FCSTD DOCUMENT  (FreeCAD 1.2R20260204 (Git shallow))
Label: RC-Robot-structure-asm
License: All rights reserved
LicenseURL: https://en.wikipedia.org/wiki/All_rights_reserved
objects: App::FeaturePython×108, App::Link×35, App::Point×1, Assembly::JointGroup×1, Assembly::AssemblyObject×1
EXTERNAL_REF file=RC-Robot-parts-export.FCStd obj=Part__Feature010
EXTERNAL_REF file=RC-Robot-parts-export.FCStd obj=Part__Feature011
EXTERNAL_REF file=RC-Robot-parts-export.FCStd obj=Part__Feature012
EXTERNAL_REF file=RC-Robot-parts-export.FCStd obj=Part__Mirroring006
EXTERNAL_REF file=RC-Robot-parts-export.FCStd obj=Part__Feature013
EXTERNAL_REF file=RC-Robot-parts-export.FCStd obj=Part__Feature015
EXTERNAL_REF file=RC-Robot-parts-export.FCStd obj=Part__Mirroring
EXTERNAL_REF file=RC-Robot-parts-export.FCStd obj=Part__Mirroring004
EXTERNAL_REF file=RC-Robot-parts-export.FCStd obj=Part__Mirroring005
EXTERNAL_REF file=RC-Robot-parts-export.FCStd obj=Part__Feature016
EXTERNAL_REF file=RC-Robot-parts-export.FCStd obj=Part__Mirroring002
EXTERNAL_REF file=RC-Robot-parts-export.FCStd obj=Part__Feature017
EXTERNAL_REF file=RC-Robot-parts-export.FCStd obj=Part__Mirroring001
EXTERNAL_REF file=RC-Robot-parts-export.FCStd obj=Part__Feature009
EXTERNAL_REF file=RC-Robot-parts-export.FCStd obj=Part
EXTERNAL_REF file=actuators-parts/wheel.FCStd obj=Part001
EXTERNAL_REF file=RC-Robot-parts-export.FCStd obj=Part__Feature004
EXTERNAL_REF file=mecanical-parts/free-wheel-support.FCStd obj=Body

FEATURE [App::Point] Origin001  label="Origine"
  Role = Origin
FEATURE [App::Link] _2020_50mm  label="2020-50mm"
  LinkPlacement = pos=(-141,2.85605,40.8027) rot=(-1,0,0;0.09388rad)
  LinkedObject = -> <external RC-Robot-parts-export.FCStd>#Part__Feature010
  Placement = pos=(-141,2.85605,40.8027) rot=(-1,0,0;0.09388rad)
FEATURE [App::Link] _2020_50mm001  label="2020-50mm001"
  LinkPlacement = pos=(-190,332.398,9.77417) rot=(0.046871,0.046871,0.997801;4.71019rad)
  LinkedObject = -> <external RC-Robot-parts-export.FCStd>#Part__Feature010
  Placement = pos=(-190,332.398,9.77417) rot=(0.046871,0.046871,0.997801;4.71019rad)
FEATURE [App::Link] _2020_300mm  label="2020-300mm"
  LinkPlacement = pos=(-176,170,-7.361e-13) rot=(1,0,0;4.71239rad)
  LinkedObject = -> <external RC-Robot-parts-export.FCStd>#Part__Feature011
  Placement = pos=(-176,170,-7.361e-13) rot=(1,0,0;4.71239rad)
FEATURE [App::Link] _2020_300mm001  label="2020-300mm001"
  LinkPlacement = pos=(-176,174.679,49.6896) rot=(1,0,0;1.38304rad)
  LinkedObject = -> <external RC-Robot-parts-export.FCStd>#Part__Feature011
  Placement = pos=(-176,174.679,49.6896) rot=(1,0,0;1.38304rad)
FEATURE [App::Link] _2020_300mm002  label="2020-300mm002"
  LinkPlacement = pos=(-556,170,-4.884e-13) rot=(-1,0,0;1.5708rad)
  LinkedObject = -> <external RC-Robot-parts-export.FCStd>#Part__Feature011
  Placement = pos=(-556,170,-4.884e-13) rot=(-1,0,0;1.5708rad)
FEATURE [App::Link] _2020_300mm003  label="2020-300mm003"
  LinkPlacement = pos=(-556,174.679,49.6896) rot=(1,0,0;4.52463rad)
  LinkedObject = -> <external RC-Robot-parts-export.FCStd>#Part__Feature011
  Placement = pos=(-556,174.679,49.6896) rot=(1,0,0;4.52463rad)
FEATURE [App::Link] _2020_300mm004  label="2020-300mm004"
  LinkPlacement = pos=(-286,170,2.72e-14) rot=(-1,0,0;1.5708rad)
  LinkedObject = -> <external RC-Robot-parts-export.FCStd>#Part__Feature011
  Placement = pos=(-286,170,2.72e-14) rot=(-1,0,0;1.5708rad)
FEATURE [App::Link] _2020_300mm005  label="2020-300mm005"
  LinkPlacement = pos=(-446,170,-2.7e-15) rot=(1,0,0;4.71239rad)
  LinkedObject = -> <external RC-Robot-parts-export.FCStd>#Part__Feature011
  Placement = pos=(-446,170,-2.7e-15) rot=(1,0,0;4.71239rad)
FEATURE [App::Link] _2020_300mm006  label="2020-300mm006"
  LinkPlacement = pos=(-286,174.679,49.6896) rot=(1,0,0;4.52463rad)
  LinkedObject = -> <external RC-Robot-parts-export.FCStd>#Part__Feature011
  Placement = pos=(-286,174.679,49.6896) rot=(1,0,0;4.52463rad)
FEATURE [App::Link] _2020_300mm007  label="2020-300mm007"
  LinkPlacement = pos=(-446,174.679,49.6896) rot=(1,0,0;4.52463rad)
  LinkedObject = -> <external RC-Robot-parts-export.FCStd>#Part__Feature011
  Placement = pos=(-446,174.679,49.6896) rot=(1,0,0;4.52463rad)
FEATURE [App::Link] _2020_340mm  label="2020-340mm"
  LinkPlacement = pos=(6.41e-14,-403,-5.59e-14) rot=(0.57735,0.57735,0.57735;2.0944rad)
  LinkedObject = -> <external RC-Robot-parts-export.FCStd>#Part__Feature012
  Placement = pos=(6.41e-14,-403,-5.59e-14) rot=(0.57735,0.57735,0.57735;2.0944rad)
FEATURE [App::Link] _2020_340mm001  label="2020-340mm001"
  LinkPlacement = pos=(1.53e-14,-67.5569,-314.496) rot=(0.093333,0.991251,-0.093333;4.7036rad)
  LinkedObject = -> <external RC-Robot-parts-export.FCStd>#Part__Feature012
  Placement = pos=(1.53e-14,-67.5569,-314.496) rot=(0.093333,0.991251,-0.093333;4.7036rad)
FEATURE [App::Link] _2020_340mm002  label="2020-340mm002"
  LinkPlacement = pos=(1.04e-14,312.134,-393.1) rot=(0.046871,0.997801,-0.046871;4.71019rad)
  LinkedObject = -> <external RC-Robot-parts-export.FCStd>#Part__Feature012
  Placement = pos=(1.04e-14,312.134,-393.1) rot=(0.046871,0.997801,-0.046871;4.71019rad)
FEATURE [App::FeaturePython] Joint  label="Fixed"  # Assembly joint (typed FeaturePython)
  Angle = 0
  AngleMax = 0
  AngleMin = 0
  Detach1 = false
  Detach2 = false
  Distance = 0
  Distance2 = 0
  EnableAngleMax = false
  EnableAngleMin = false
  EnableLengthMax = false
  EnableLengthMin = false
  JointType = 0 (Fixed)
  LengthMax = 0
  LengthMin = 0
  Offset2 = pos=(0,0,170) rot=(0,0,1;0rad)
  Placement1 = pos=(403,1.007e-13,170) rot=(0,0,1;0rad)
  Placement2 = pos=(0,0,170) rot=(0,0,1;0rad)
  Reference1 = -> _2020_340mm [Face50,Edge6]
  Reference2 = -> Origin [YZ_Plane.,YZ_Plane.]
  Suppressed = false
FEATURE [App::FeaturePython] GroundedJoint  # Assembly grounded joint (typed FeaturePython)
  ObjectToGround = -> _2020_340mm
FEATURE [App::Link] CoinLateralBD
  LinkPlacement = pos=(180,64.583,-54.9907) rot=(0.046871,-0.046871,0.997801;1.573rad)
  LinkedObject = -> <external RC-Robot-parts-export.FCStd>#Part__Mirroring006
  Placement = pos=(180,64.583,-54.9907) rot=(0.046871,-0.046871,0.997801;1.573rad)
FEATURE [App::FeaturePython] Joint001  label="Revolute002"  # Assembly joint (typed FeaturePython)
  Angle = 0
  AngleMax = 0
  AngleMin = 0
  Detach1 = false
  Detach2 = false
  Distance = 0
  Distance2 = 0
  EnableAngleMax = false
  EnableAngleMin = false
  EnableLengthMax = false
  EnableLengthMin = false
  JointType = 1 (Revolute)
  LengthMax = 0
  LengthMin = 0
  Placement1 = pos=(-59.1437,10,60.8027) rot=(0.066432,-0.705545,0.705545;3.00892rad)
  Placement2 = pos=(403,1.007e-13,170) rot=(0,0,1;0rad)
  Reference1 = -> CoinLateralBD [Edge7,Edge7]
  Reference2 = -> _2020_340mm [Edge52,Edge52]
  Suppressed = false
FEATURE [App::FeaturePython] Joint002  label="Parallel002"  # Assembly joint (typed FeaturePython)
  Angle = 0
  AngleMax = 0
  AngleMin = 0
  Detach1 = false
  Detach2 = false
  Distance = 0
  Distance2 = 0
  EnableAngleMax = false
  EnableAngleMin = false
  EnableLengthMax = false
  EnableLengthMin = false
  JointType = 6 (Parallel)
  LengthMax = 0
  LengthMin = 0
  Placement1 = pos=(-68.1623,30,71.6961) rot=(-0.046923,0,-0.998899;3.14159rad)
  Placement2 = pos=(398.1,10,170) rot=(-0.57735,-0.57735,-0.57735;2.0944rad)
  Reference1 = -> CoinLateralBD [Face8,Vertex15]
  Reference2 = -> _2020_340mm [Face22,Vertex40]
  Suppressed = false
FEATURE [App::FeaturePython] Joint004  label="Distance002"  # Assembly joint (typed FeaturePython)
  Angle = 0
  AngleMax = 0
  AngleMin = 0
  Detach1 = false
  Detach2 = false
  Distance = 0
  Distance2 = 0
  EnableAngleMax = false
  EnableAngleMin = false
  EnableLengthMax = false
  EnableLengthMin = false
  JointType = 5 (Distance)
  LengthMax = 0
  LengthMin = 0
  Placement1 = pos=(321,6.7,7.1e-15) rot=(0,1,0;1.5708rad)
  Placement2 = pos=(-58.1674,3.411e-13,86.3477) rot=(0.505206,0.610232,-0.610232;2.20599rad)
  Reference1 = -> _2020_50mm [Face26,Vertex37]
  Reference2 = -> CoinLateralBD [Face28,Face28]
  Suppressed = false
FEATURE [App::FeaturePython] Joint005  label="Distance003"  # Assembly joint (typed FeaturePython)
  Angle = 0
  AngleMax = 0
  AngleMin = 0
  Detach1 = false
  Detach2 = false
  Distance = 0
  Distance2 = 0
  EnableAngleMax = false
  EnableAngleMin = false
  EnableLengthMax = false
  EnableLengthMin = false
  JointType = 5 (Distance)
  LengthMax = 0
  LengthMin = 0
  Placement1 = pos=(331,1.13e-14,-25) rot=(0,0,1;0rad)
  Placement2 = pos=(-57.1418,-10,76.5974) rot=(0,-1,0;2.95383rad)
  Reference1 = -> _2020_50mm [Face51,Vertex66]
  Reference2 = -> CoinLateralBD [Face19,Face19]
  Suppressed = false
FEATURE [App::FeaturePython] Joint006  label="Distance004"  # Assembly joint (typed FeaturePython)
  Angle = 0
  AngleMax = 0
  AngleMin = 0
  Detach1 = false
  Detach2 = false
  Distance = 0
  Distance2 = 0
  EnableAngleMax = false
  EnableAngleMin = false
  EnableLengthMax = false
  EnableLengthMin = false
  JointType = 5 (Distance)
  LengthMax = 0
  LengthMin = 0
  Placement1 = pos=(-45.4509,-10,84.5551) rot=(0,1,0;1.75856rad)
  Placement2 = pos=(337.7,10,-7.1e-15) rot=(0.57735,0.57735,0.57735;4.18879rad)
  Reference1 = -> CoinLateralBD [Face20,Edge1]
  Reference2 = -> _2020_50mm [Face2,Vertex54]
  Suppressed = false
FEATURE [App::FeaturePython] Joint007  label="Distance006"  # Assembly joint (typed FeaturePython)
  Angle = 0
  AngleMax = 0
  AngleMin = 0
  Detach1 = false
  Detach2 = false
  Distance = 0
  Distance2 = 0
  EnableAngleMax = false
  EnableAngleMin = false
  EnableLengthMax = false
  EnableLengthMin = false
  JointType = 5 (Distance)
  LengthMax = 0
  LengthMin = 0
  Placement1 = pos=(366,4.6e-15,-150) rot=(0,0,1;0rad)
  Placement2 = pos=(-39.2318,-10,58.9279) rot=(0,-1,0;1.47692rad)
  Reference1 = -> _2020_300mm [Face51,Vertex62]
  Reference2 = -> CoinLateralBD [Face18,Face18]
  Suppressed = false
FEATURE [App::FeaturePython] Joint008  label="Distance007"  # Assembly joint (typed FeaturePython)
  Angle = 0
  AngleMax = 0
  AngleMin = 0
  Detach1 = false
  Detach2 = false
  Distance = 0
  Distance2 = 0
  EnableAngleMax = false
  EnableAngleMin = false
  EnableLengthMax = false
  EnableLengthMin = false
  JointType = 5 (Distance)
  LengthMax = 0
  LengthMin = 0
  Placement1 = pos=(359.3,-10,4.547e-13) rot=(0.57735,0.57735,0.57735;4.18879rad)
  Placement2 = pos=(-28.3384,-10,67.9464) rot=(0,1,0;0.09388rad)
  Reference1 = -> _2020_300mm [Face49,Vertex100]
  Reference2 = -> CoinLateralBD [Face21,Vertex44]
  Suppressed = false
FEATURE [App::FeaturePython] Joint009  label="Distance008"  # Assembly joint (typed FeaturePython)
  Angle = 0
  AngleMax = 0
  AngleMin = 0
  Detach1 = false
  Detach2 = false
  Distance = 0
  Distance2 = 0
  EnableAngleMax = false
  EnableAngleMin = false
  EnableLengthMax = false
  EnableLengthMin = false
  JointType = 5 (Distance)
  LengthMax = 0
  LengthMin = 0
  Placement1 = pos=(376,-6.7,4.832e-13) rot=(0,-1,0;1.5708rad)
  Placement2 = pos=(-45.367,-20,69.775) rot=(0.505206,0.610232,-0.610232;2.20599rad)
  Reference1 = -> _2020_300mm [Face25,Vertex77]
  Reference2 = -> CoinLateralBD [Face11,Face11]
  Suppressed = false
FEATURE [App::Link] CoinLateralHD
  LinkPlacement = pos=(180,64.583,34.9907) rot=(-0.046871,0.046871,0.997801;1.573rad)
  LinkedObject = -> <external RC-Robot-parts-export.FCStd>#Part__Feature013
  Placement = pos=(180,64.583,34.9907) rot=(-0.046871,0.046871,0.997801;1.573rad)
FEATURE [App::FeaturePython] Joint010  label="Distance009"  # Assembly joint (typed FeaturePython)
  Angle = 0
  AngleMax = 0
  AngleMin = 0
  Detach1 = false
  Detach2 = false
  Distance = 0
  Distance2 = 0
  EnableAngleMax = false
  EnableAngleMin = false
  EnableLengthMax = false
  EnableLengthMin = false
  JointType = 5 (Distance)
  LengthMax = 0
  LengthMin = 0
  Placement1 = pos=(-62,-10,25) rot=(0,-1,0;3.14159rad)
  Placement2 = pos=(331,-4.9e-15,25) rot=(0,1,0;3.14159rad)
  Reference1 = -> CoinLateralHD [Face19,Face19]
  Reference2 = -> _2020_50mm [Face1,Vertex8]
  Suppressed = false
FEATURE [App::FeaturePython] Joint011  label="Distance010"  # Assembly joint (typed FeaturePython)
  Angle = 0
  AngleMax = 0
  AngleMin = 0
  Detach1 = false
  Detach2 = false
  Distance = 0
  Distance2 = 0
  EnableAngleMax = false
  EnableAngleMin = false
  EnableLengthMax = false
  EnableLengthMin = false
  JointType = 5 (Distance)
  LengthMax = 0
  LengthMin = 0
  Placement1 = pos=(-49.1588,-20,29.5047) rot=(-0.57735,-0.57735,-0.57735;2.0944rad)
  Placement2 = pos=(341,6.7,-2.13e-14) rot=(0,-1,0;1.5708rad)
  Reference1 = -> CoinLateralHD [Face11,Vertex24]
  Reference2 = -> _2020_50mm [Face5,Vertex3]
  Suppressed = false
FEATURE [App::FeaturePython] Joint012  label="Distance011"  # Assembly joint (typed FeaturePython)
  Angle = 0
  AngleMax = 0
  AngleMin = 0
  Detach1 = false
  Detach2 = false
  Distance = 0
  Distance2 = 0
  EnableAngleMax = false
  EnableAngleMin = false
  EnableLengthMax = false
  EnableLengthMin = false
  JointType = 5 (Distance)
  LengthMax = 0
  LengthMin = 0
  Placement1 = pos=(-72,10.4414,17.0721) rot=(-0.57735,-0.57735,0.57735;2.0944rad)
  Placement2 = pos=(324.3,-10,-1.42e-14) rot=(0.57735,0.57735,0.57735;4.18879rad)
  Reference1 = -> CoinLateralHD [Face25,Face25]
  Reference2 = -> _2020_50mm [Face49,Vertex26]
  Suppressed = false
FEATURE [App::FeaturePython] Joint013  label="Parallel004"  # Assembly joint (typed FeaturePython)
  Angle = 0
  AngleMax = 0
  AngleMin = 0
  Detach1 = false
  Detach2 = false
  Distance = 0
  Distance2 = 0
  EnableAngleMax = false
  EnableAngleMin = false
  EnableLengthMax = false
  EnableLengthMin = false
  JointType = 6 (Parallel)
  LengthMax = 0
  LengthMin = 0
  Placement1 = pos=(368.84,-3.9,150) rot=(0,1,0;3.14159rad)
  Placement2 = pos=(-41.1066,-10,39.0159) rot=(0,-1,0;4.61851rad)
  Reference1 = -> _2020_300mm001 [Face1,Vertex20]
  Reference2 = -> CoinLateralHD [Face18,Face18]
  Suppressed = false
FEATURE [App::FeaturePython] Joint014  label="Distance014"  # Assembly joint (typed FeaturePython)
  Angle = 0
  AngleMax = 0
  AngleMin = 0
  Detach1 = false
  Detach2 = false
  Distance = 0
  Distance2 = 0
  EnableAngleMax = false
  EnableAngleMin = false
  EnableLengthMax = false
  EnableLengthMin = false
  JointType = 5 (Distance)
  LengthMax = 0
  LengthMin = 0
  Placement1 = pos=(376,-6.7,4.547e-13) rot=(0,-1,0;1.5708rad)
  Placement2 = pos=(-49.1588,-20,29.5047) rot=(-0.57735,-0.57735,-0.57735;2.0944rad)
  Reference1 = -> _2020_300mm001 [Face25,Vertex14]
  Reference2 = -> CoinLateralHD [Face11,Vertex21]
  Suppressed = false
FEATURE [App::FeaturePython] Joint015  label="Distance015"  # Assembly joint (typed FeaturePython)
  Angle = 0
  AngleMax = 0
  AngleMin = 0
  Detach1 = false
  Detach2 = false
  Distance = 0
  Distance2 = 0
  EnableAngleMax = false
  EnableAngleMin = false
  EnableLengthMax = false
  EnableLengthMin = false
  JointType = 5 (Distance)
  LengthMax = 0
  LengthMin = 0
  Placement1 = pos=(-32.0881,-10,28.1226) rot=(0,1,0;0.09388rad)
  Placement2 = pos=(372.7,-10,-4.832e-13) rot=(-0.57735,-0.57735,-0.57735;2.0944rad)
  Reference1 = -> CoinLateralHD [Face21,Vertex44]
  Reference2 = -> _2020_300mm001 [Face29,Vertex15]
  Suppressed = false
FEATURE [App::FeaturePython] Joint016  label="Distance016"  # Assembly joint (typed FeaturePython)
  Angle = 0
  AngleMax = 0
  AngleMin = 0
  Detach1 = false
  Detach2 = false
  Distance = 0
  Distance2 = 0
  EnableAngleMax = false
  EnableAngleMin = false
  EnableLengthMax = false
  EnableLengthMin = false
  JointType = 5 (Distance)
  LengthMax = 0
  LengthMin = 0
  Placement1 = pos=(366,-1.42e-14,150) rot=(0,1,0;3.14159rad)
  Placement2 = pos=(-41.1066,-10,39.0159) rot=(0,-1,0;4.61851rad)
  Reference1 = -> _2020_300mm001 [Face1,Edge2]
  Reference2 = -> CoinLateralHD [Face18,Face18]
  Suppressed = false
FEATURE [App::FeaturePython] Joint017  label="Parallel005"  # Assembly joint (typed FeaturePython)
  Angle = 0
  AngleMax = 0
  AngleMin = 0
  Detach1 = false
  Detach2 = false
  Distance = 0
  Distance2 = 0
  EnableAngleMax = false
  EnableAngleMin = false
  EnableLengthMax = false
  EnableLengthMin = false
  JointType = 6 (Parallel)
  LengthMax = 0
  LengthMin = 0
  Placement1 = pos=(407.9,-10,-170) rot=(0.57735,0.57735,0.57735;4.18879rad)
  Placement2 = pos=(-70.9745,-5,41.8282) rot=(0.673149,0,-0.739507;3.14159rad)
  Reference1 = -> _2020_340mm001 [Face29,Vertex81]
  Reference2 = -> CoinLateralHD [Face7,Face7]
  Suppressed = false
FEATURE [App::FeaturePython] Joint018  label="Distance017"  # Assembly joint (typed FeaturePython)
  Angle = 0
  AngleMax = 0
  AngleMin = 0
  Detach1 = false
  Detach2 = false
  Distance = 0
  Distance2 = 0
  EnableAngleMax = false
  EnableAngleMin = false
  EnableLengthMax = false
  EnableLengthMin = false
  JointType = 5 (Distance)
  LengthMax = 0
  LengthMin = 0
  Placement1 = pos=(409.7,-10,-5.945e-13) rot=(0.57735,0.57735,0.57735;4.18879rad)
  Placement2 = pos=(-70.9745,-5,41.8282) rot=(0.673149,0,-0.739507;3.14159rad)
  Reference1 = -> _2020_340mm001 [Face29,Vertex79]
  Reference2 = -> CoinLateralHD [Face7,Face7]
  Suppressed = false
FEATURE [App::FeaturePython] Joint019  label="Distance018"  # Assembly joint (typed FeaturePython)
  Angle = 0
  AngleMax = 0
  AngleMin = 0
  Detach1 = false
  Detach2 = false
  Distance = 0
  Distance2 = 0
  EnableAngleMax = false
  EnableAngleMin = false
  EnableLengthMax = false
  EnableLengthMin = false
  JointType = 5 (Distance)
  LengthMax = 0
  LengthMin = 0
  Placement1 = pos=(393,-6.7,-1.13e-14) rot=(0,1,0;1.5708rad)
  Placement2 = pos=(-61.956,20,30.9348) rot=(-0.046923,0,-0.998899;3.14159rad)
  Reference1 = -> _2020_340mm001 [Face46,Vertex96]
  Reference2 = -> CoinLateralHD [Face8,Face8]
  Suppressed = false
FEATURE [App::FeaturePython] Joint020  label="Distance019"  # Assembly joint (typed FeaturePython)
  Angle = 0
  AngleMax = 0
  AngleMin = 0
  Detach1 = false
  Detach2 = false
  Distance = 0
  Distance2 = 0
  EnableAngleMax = false
  EnableAngleMin = false
  EnableLengthMax = false
  EnableLengthMin = false
  JointType = 5 (Distance)
  LengthMax = 0
  LengthMin = 0
  Placement1 = pos=(403,-1.87e-14,-170) rot=(0,0,1;0rad)
  Placement2 = pos=(-61.0185,10,40.8908) rot=(-0.57735,-0.57735,-0.57735;2.0944rad)
  Reference1 = -> _2020_340mm001 [Face51,Edge2]
  Reference2 = -> CoinLateralHD [Face5,Vertex7]
  Suppressed = false
FEATURE [App::Link] CoinAvant001
  LinkPlacement = pos=(180,64.583,34.9907) rot=(-0.046871,0.046871,0.997801;1.573rad)
  LinkedObject = -> <external RC-Robot-parts-export.FCStd>#Part__Feature015
  Placement = pos=(180,64.583,34.9907) rot=(-0.046871,0.046871,0.997801;1.573rad)
FEATURE [App::FeaturePython] Joint040  label="Distance040"  # Assembly joint (typed FeaturePython)
  Angle = 0
  AngleMax = 0
  AngleMin = 0
  Detach1 = false
  Detach2 = false
  Distance = 0
  Distance2 = 0
  EnableAngleMax = false
  EnableAngleMin = false
  EnableLengthMax = false
  EnableLengthMin = false
  JointType = 5 (Distance)
  LengthMax = 0
  LengthMin = 0
  Placement1 = pos=(257.479,-10,-9.89779) rot=(0,1,0;1.47692rad)
  Placement2 = pos=(366,-8.5e-15,150) rot=(0,1,0;3.14159rad)
  Reference1 = -> CoinAvant001 [Face32,Vertex62]
  Reference2 = -> _2020_300mm [Face1,Edge26]
  Suppressed = false
FEATURE [App::FeaturePython] Joint041  label="Distance041"  # Assembly joint (typed FeaturePython)
  Angle = 0
  AngleMax = 0
  AngleMin = 0
  Detach1 = false
  Detach2 = false
  Distance = 0
  Distance2 = 0
  EnableAngleMax = false
  EnableAngleMin = false
  EnableLengthMax = false
  EnableLengthMin = false
  JointType = 5 (Distance)
  LengthMax = 0
  LengthMin = 0
  Placement1 = pos=(247.472,5.68e-14,1.91918e-11) rot=(-0.57735,-0.57735,-0.57735;2.0944rad)
  Placement2 = pos=(356,6.7,-2.84e-14) rot=(0,1,0;1.5708rad)
  Reference1 = -> CoinAvant001 [Face25,Face25]
  Reference2 = -> _2020_300mm [Face26,Vertex38]
  Suppressed = false
FEATURE [App::FeaturePython] Joint042  label="Distance042"  # Assembly joint (typed FeaturePython)
  Angle = 0
  AngleMax = 0
  AngleMin = 0
  Detach1 = false
  Detach2 = false
  Distance = 0
  Distance2 = 0
  EnableAngleMax = false
  EnableAngleMin = false
  EnableLengthMax = false
  EnableLengthMin = false
  JointType = 5 (Distance)
  LengthMax = 0
  LengthMin = 0
  Placement1 = pos=(253.559,2.3039,-21.3154) rot=(0,1,0;3.04771rad)
  Placement2 = pos=(359.3,10,0) rot=(0.57735,0.57735,0.57735;4.18879rad)
  Reference1 = -> CoinAvant001 [Face15,Face15]
  Reference2 = -> _2020_300mm [Face22,Vertex39]
  Suppressed = false
FEATURE [App::FeaturePython] Joint043  label="Parallel011"  # Assembly joint (typed FeaturePython)
  Angle = 0
  AngleMax = 0
  AngleMin = 0
  Detach1 = false
  Detach2 = false
  Distance = 0
  Distance2 = 0
  EnableAngleMax = false
  EnableAngleMin = false
  EnableLengthMax = false
  EnableLengthMin = false
  JointType = 6 (Parallel)
  LengthMax = 0
  LengthMin = 0
  Placement1 = pos=(394.5,10,-170) rot=(0.57735,0.57735,0.57735;4.18879rad)
  Placement2 = pos=(296.591,12.5,-1.0019e-12) rot=(0.707107,0,0.707107;3.14159rad)
  Reference1 = -> _2020_340mm002 [Face22,Vertex74]
  Reference2 = -> CoinAvant001 [Face7,Face7]
  Suppressed = false
FEATURE [App::Link] CoinAvant__Mirror__1_  label="CoinAvant (Mirror #1)"
  LinkPlacement = pos=(-160,64.583,34.9907) rot=(-0.046871,0.046871,0.997801;1.573rad)
  LinkedObject = -> <external RC-Robot-parts-export.FCStd>#Part__Mirroring
  Placement = pos=(-160,64.583,34.9907) rot=(-0.046871,0.046871,0.997801;1.573rad)
FEATURE [App::FeaturePython] Joint044  label="Fixed003"  # Assembly joint (typed FeaturePython)
  Angle = 0
  AngleMax = 0
  AngleMin = 0
  Detach1 = false
  Detach2 = false
  Distance = 0
  Distance2 = 0
  EnableAngleMax = false
  EnableAngleMin = false
  EnableLengthMax = false
  EnableLengthMin = false
  JointType = 0 (Fixed)
  LengthMax = 0
  LengthMin = 0
  Placement1 = pos=(403,1.137e-13,-170) rot=(0,0,1;0rad)
  Placement2 = pos=(286.591,10,2.84e-14) rot=(0,-0.707107,-0.707107;3.14159rad)
  Reference1 = -> _2020_340mm002 [Edge150,Edge150]
  Reference2 = -> CoinAvant001 [Edge17,Edge17]
  Suppressed = false
FEATURE [App::FeaturePython] Joint045  label="Parallel014"  # Assembly joint (typed FeaturePython)
  Angle = 0
  AngleMax = 0
  AngleMin = 0
  Detach1 = false
  Detach2 = false
  Distance = 0
  Distance2 = 0
  EnableAngleMax = false
  EnableAngleMin = false
  EnableLengthMax = false
  EnableLengthMin = false
  JointType = 6 (Parallel)
  LengthMax = 0
  LengthMin = 0
  Placement1 = pos=(411.5,10,170) rot=(0.57735,0.57735,0.57735;4.18879rad)
  Placement2 = pos=(296.591,7.5,-1.0019e-12) rot=(0,-1,0;1.5708rad)
  Reference1 = -> _2020_340mm002 [Face2,Vertex1]
  Reference2 = -> CoinAvant__Mirror__1_ [Face7,Face7]
  Suppressed = false
FEATURE [App::FeaturePython] Joint046  label="Fixed004"  # Assembly joint (typed FeaturePython)
  Angle = 0
  AngleMax = 0
  AngleMin = 0
  Detach1 = false
  Detach2 = false
  Distance = 0
  Distance2 = 0
  EnableAngleMax = false
  EnableAngleMin = false
  EnableLengthMax = false
  EnableLengthMin = false
  JointType = 0 (Fixed)
  LengthMax = 0
  LengthMin = 0
  Placement1 = pos=(286.591,10,2.13e-14) rot=(0,-0.707107,-0.707107;3.14159rad)
  Placement2 = pos=(403,0,170) rot=(0,0,1;0rad)
  Reference1 = -> CoinAvant__Mirror__1_ [Edge17,Edge17]
  Reference2 = -> _2020_340mm002 [Edge51,Edge51]
  Suppressed = false
FEATURE [App::FeaturePython] Joint047  label="Parallel015"  # Assembly joint (typed FeaturePython)
  Angle = 0
  AngleMax = 0
  AngleMin = 0
  Detach1 = false
  Detach2 = false
  Distance = 0
  Distance2 = 0
  EnableAngleMax = false
  EnableAngleMin = false
  EnableLengthMax = false
  EnableLengthMin = false
  JointType = 6 (Parallel)
  LengthMax = 0
  LengthMin = 0
  Placement1 = pos=(360.5,8.2,150) rot=(0,1,0;3.14159rad)
  Placement2 = pos=(257.479,30,-9.89779) rot=(0.739507,0,-0.673149;3.14159rad)
  Reference1 = -> _2020_300mm002 [Face1,Vertex42]
  Reference2 = -> CoinAvant__Mirror__1_ [Face32,Face32]
  Suppressed = false
FEATURE [App::FeaturePython] Joint048  label="Parallel016"  # Assembly joint (typed FeaturePython)
  Angle = 0
  AngleMax = 0
  AngleMin = 0
  Detach1 = false
  Detach2 = false
  Distance = 0
  Distance2 = 0
  EnableAngleMax = false
  EnableAngleMin = false
  EnableLengthMax = false
  EnableLengthMin = false
  JointType = 6 (Parallel)
  LengthMax = 0
  LengthMin = 0
  Placement1 = pos=(357.5,-8.5,150) rot=(0,1,0;3.14159rad)
  Placement2 = pos=(257.479,30,9.89779) rot=(0.673149,0,-0.739507;3.14159rad)
  Reference1 = -> _2020_300mm003 [Face1,Edge26]
  Reference2 = -> CoinAvant__Mirror__1_ [Face34,Face34]
  Suppressed = false
FEATURE [App::FeaturePython] Joint049  label="Distance047"  # Assembly joint (typed FeaturePython)
  Angle = 0
  AngleMax = 0
  AngleMin = 0
  Detach1 = false
  Detach2 = false
  Distance = 0
  Distance2 = 0
  EnableAngleMax = false
  EnableAngleMin = false
  EnableLengthMax = false
  EnableLengthMin = false
  JointType = 5 (Distance)
  LengthMax = 0
  LengthMin = 0
  Placement1 = pos=(253.559,17.6961,21.3154) rot=(0.998899,0,-0.046923;3.14159rad)
  Placement2 = pos=(372.7,-10,-4.547e-13) rot=(-0.57735,-0.57735,-0.57735;2.0944rad)
  Reference1 = -> CoinAvant__Mirror__1_ [Face4,Vertex16]
  Reference2 = -> _2020_300mm003 [Face29,Vertex15]
  Suppressed = false
FEATURE [App::FeaturePython] Joint050  label="Distance048"  # Assembly joint (typed FeaturePython)
  Angle = 0
  AngleMax = 0
  AngleMin = 0
  Detach1 = false
  Detach2 = false
  Distance = 0
  Distance2 = 0
  EnableAngleMax = false
  EnableAngleMin = false
  EnableLengthMax = false
  EnableLengthMin = false
  JointType = 5 (Distance)
  LengthMax = 0
  LengthMin = 0
  Placement1 = pos=(253.559,17.6961,-21.3154) rot=(0.046923,0,-0.998899;3.14159rad)
  Placement2 = pos=(372.7,10,0) rot=(0.57735,0.57735,0.57735;4.18879rad)
  Reference1 = -> CoinAvant__Mirror__1_ [Face15,Vertex9]
  Reference2 = -> _2020_300mm002 [Face2,Vertex2]
  Suppressed = false
FEATURE [App::FeaturePython] Joint051  label="Distance049"  # Assembly joint (typed FeaturePython)
  Angle = 0
  AngleMax = 0
  AngleMin = 0
  Detach1 = false
  Detach2 = false
  Distance = 0
  Distance2 = 0
  EnableAngleMax = false
  EnableAngleMin = false
  EnableLengthMax = false
  EnableLengthMin = false
  JointType = 5 (Distance)
  LengthMax = 0
  LengthMin = 0
  Placement1 = pos=(366,0,150) rot=(0,1,0;3.14159rad)
  Placement2 = pos=(257.479,30,9.89779) rot=(0.673149,0,-0.739507;3.14159rad)
  Reference1 = -> _2020_300mm003 [Face1,Vertex42]
  Reference2 = -> CoinAvant__Mirror__1_ [Face34,Face34]
  Suppressed = false
FEATURE [App::FeaturePython] Joint052  label="Distance050"  # Assembly joint (typed FeaturePython)
  Angle = 0
  AngleMax = 0
  AngleMin = 0
  Detach1 = false
  Detach2 = false
  Distance = 0
  Distance2 = 0
  EnableAngleMax = false
  EnableAngleMin = false
  EnableLengthMax = false
  EnableLengthMin = false
  JointType = 5 (Distance)
  LengthMax = 0
  LengthMin = 0
  Placement1 = pos=(366,-1.5e-15,150) rot=(0,1,0;3.14159rad)
  Placement2 = pos=(257.479,30,-9.89779) rot=(0.739507,0,-0.673149;3.14159rad)
  Reference1 = -> _2020_300mm002 [Face1,Edge2]
  Reference2 = -> CoinAvant__Mirror__1_ [Face32,Face32]
  Suppressed = false
FEATURE [App::Link] CoinLateralHG
  LinkPlacement = pos=(-220,64.583,34.9907) rot=(-0.046871,0.046871,0.997801;1.573rad)
  LinkedObject = -> <external RC-Robot-parts-export.FCStd>#Part__Mirroring004
  Placement = pos=(-220,64.583,34.9907) rot=(-0.046871,0.046871,0.997801;1.573rad)
FEATURE [App::FeaturePython] Joint053  label="Parallel017"  # Assembly joint (typed FeaturePython)
  Angle = 0
  AngleMax = 0
  AngleMin = 0
  Detach1 = false
  Detach2 = false
  Distance = 0
  Distance2 = 0
  EnableAngleMax = false
  EnableAngleMin = false
  EnableLengthMax = false
  EnableLengthMin = false
  JointType = 6 (Parallel)
  LengthMax = 0
  LengthMin = 0
  Placement1 = pos=(-70.9745,-35,41.8282) rot=(0,1,0;1.66468rad)
  Placement2 = pos=(411.5,-10,170) rot=(0.57735,0.57735,0.57735;4.18879rad)
  Reference1 = -> CoinLateralHG [Face7,Face7]
  Reference2 = -> _2020_340mm001 [Face29,Vertex15]
  Suppressed = false
FEATURE [App::FeaturePython] Joint054  label="Distance051"  # Assembly joint (typed FeaturePython)
  Angle = 0
  AngleMax = 0
  AngleMin = 0
  Detach1 = false
  Detach2 = false
  Distance = 0
  Distance2 = 0
  EnableAngleMax = false
  EnableAngleMin = false
  EnableLengthMax = false
  EnableLengthMin = false
  JointType = 5 (Distance)
  LengthMax = 0
  LengthMin = 0
  Placement1 = pos=(-70.9745,-35,41.8282) rot=(0,1,0;1.66468rad)
  Placement2 = pos=(409.7,-10,-5.945e-13) rot=(0.57735,0.57735,0.57735;4.18879rad)
  Reference1 = -> CoinLateralHG [Face7,Face7]
  Reference2 = -> _2020_340mm001 [Face29,Vertex16]
  Suppressed = false
FEATURE [App::FeaturePython] Joint055  label="Fixed005"  # Assembly joint (typed FeaturePython)
  Angle = 0
  AngleMax = 0
  AngleMin = 0
  Detach1 = false
  Detach2 = false
  Distance = 0
  Distance2 = 0
  EnableAngleMax = false
  EnableAngleMin = false
  EnableLengthMax = false
  EnableLengthMin = false
  JointType = 0 (Fixed)
  LengthMax = 0
  LengthMin = 0
  Placement1 = pos=(-61.0185,-50,40.8908) rot=(0,-0.707107,-0.707107;3.14159rad)
  Placement2 = pos=(403,6.22e-14,170) rot=(0,0,1;0rad)
  Reference1 = -> CoinLateralHG [Edge7,Edge7]
  Reference2 = -> _2020_340mm001 [Edge51,Edge51]
  Suppressed = false
FEATURE [App::FeaturePython] Joint056  label="Fixed006"  # Assembly joint (typed FeaturePython)
  Angle = 0
  AngleMax = 0
  AngleMin = 0
  Detach1 = false
  Detach2 = false
  Distance = 0
  Distance2 = 0
  EnableAngleMax = false
  EnableAngleMin = false
  EnableLengthMax = false
  EnableLengthMin = false
  JointType = 0 (Fixed)
  LengthMax = 0
  LengthMin = 0
  Placement1 = pos=(331,-2.84e-14,25) rot=(0,0,1;0rad)
  Placement2 = pos=(-62,-30,25) rot=(0,0,-1;3.14159rad)
  Reference1 = -> _2020_50mm001 [Edge51,Edge51]
  Reference2 = -> CoinLateralHG [Face19,Face19]
  Suppressed = false
FEATURE [App::Link] CoinLateralBG
  LinkPlacement = pos=(-220,49.6781,103.309) rot=(0.046871,-0.046871,0.997801;1.573rad)
  LinkedObject = -> <external RC-Robot-parts-export.FCStd>#Part__Mirroring005
  Placement = pos=(-220,49.6781,103.309) rot=(0.046871,-0.046871,0.997801;1.573rad)
FEATURE [App::FeaturePython] Joint057  label="Fixed007"  # Assembly joint (typed FeaturePython)
  Angle = 0
  AngleMax = 0
  AngleMin = 0
  Detach1 = false
  Detach2 = false
  Distance = 0
  Distance2 = 0
  EnableAngleMax = false
  EnableAngleMin = false
  EnableLengthMax = false
  EnableLengthMin = false
  JointType = 0 (Fixed)
  LengthMax = 0
  LengthMin = 0
  Placement1 = pos=(-57.1418,-30,-82.4026) rot=(-0.093742,0,-0.995597;3.14159rad)
  Placement2 = pos=(331,-2.84e-14,-25) rot=(0,0,1;0rad)
  Reference1 = -> CoinLateralBG [Face19,Face19]
  Reference2 = -> _2020_50mm001 [Edge152,Edge152]
  Suppressed = false
FEATURE [App::Link] CoinInterieurArriere001
  LinkPlacement = pos=(70,64.583,34.9907) rot=(-0.046871,0.046871,0.997801;1.573rad)
  LinkedObject = -> <external RC-Robot-parts-export.FCStd>#Part__Feature016
  Placement = pos=(70,64.583,34.9907) rot=(-0.046871,0.046871,0.997801;1.573rad)
FEATURE [App::Link] CoinInterieurArriere__Mirror__3_  label="CoinInterieurArriere (Mirror #3)"
  LinkPlacement = pos=(-124,64.583,34.9907) rot=(-0.046871,0.046871,0.997801;1.573rad)
  LinkedObject = -> <external RC-Robot-parts-export.FCStd>#Part__Mirroring002
  Placement = pos=(-124,64.583,34.9907) rot=(-0.046871,0.046871,0.997801;1.573rad)
FEATURE [App::FeaturePython] Joint058  label="Distance053"  # Assembly joint (typed FeaturePython)
  Angle = 0
  AngleMax = 0
  AngleMin = 0
  Detach1 = false
  Detach2 = false
  Distance = 0
  Distance2 = 0
  EnableAngleMax = false
  EnableAngleMin = false
  EnableLengthMax = false
  EnableLengthMin = false
  JointType = 5 (Distance)
  LengthMax = 0
  LengthMin = 0
  Placement1 = pos=(-72.24,-13.5,-28.3876) rot=(-0.673149,0,-0.739507;3.14159rad)
  Placement2 = pos=(393,6.7,-1.293e-13) rot=(0,1,0;1.5708rad)
  Reference1 = -> CoinInterieurArriere001 [Face21,Face21]
  Reference2 = -> _2020_340mm [Face26,Vertex37]
  Suppressed = false
FEATURE [App::FeaturePython] Joint059  label="Distance054"  # Assembly joint (typed FeaturePython)
  Angle = 0
  AngleMax = 0
  AngleMin = 0
  Detach1 = false
  Detach2 = false
  Distance = 0
  Distance2 = 0
  EnableAngleMax = false
  EnableAngleMin = false
  EnableLengthMax = false
  EnableLengthMin = false
  JointType = 5 (Distance)
  LengthMax = 0
  LengthMin = 0
  Placement1 = pos=(-61.838,-13.856,-30.9237) rot=(0.706717,0.706717,0.033198;3.07522rad)
  Placement2 = pos=(396.3,10,-1.312e-13) rot=(-0.57735,-0.57735,-0.57735;2.0944rad)
  Reference1 = -> CoinInterieurArriere001 [Face18,Face18]
  Reference2 = -> _2020_340mm [Face22,Vertex40]
  Suppressed = false
FEATURE [App::FeaturePython] Joint060  label="Distance055"  # Assembly joint (typed FeaturePython)
  Angle = 0
  AngleMax = 0
  AngleMin = 0
  Detach1 = false
  Detach2 = false
  Distance = 0
  Distance2 = 0
  EnableAngleMax = false
  EnableAngleMin = false
  EnableLengthMax = false
  EnableLengthMin = false
  JointType = 5 (Distance)
  LengthMax = 0
  LengthMin = 0
  Placement1 = pos=(-61.838,-40.144,-30.9237) rot=(0.046871,-0.046871,-0.997801;1.573rad)
  Placement2 = pos=(409.7,10,-1.367e-13) rot=(-0.57735,-0.57735,-0.57735;2.0944rad)
  Reference1 = -> CoinInterieurArriere__Mirror__3_ [Face18,Face18]
  Reference2 = -> _2020_340mm [Face2,Vertex53]
  Suppressed = false
FEATURE [App::FeaturePython] Joint061  label="Distance056"  # Assembly joint (typed FeaturePython)
  Angle = 0
  AngleMax = 0
  AngleMin = 0
  Detach1 = false
  Detach2 = false
  Distance = 0
  Distance2 = 0
  EnableAngleMax = false
  EnableAngleMin = false
  EnableLengthMax = false
  EnableLengthMin = false
  JointType = 5 (Distance)
  LengthMax = 0
  LengthMin = 0
  Placement1 = pos=(-51.0661,-41.4525,-39.916) rot=(0,-1,0;4.80627rad)
  Placement2 = pos=(413,6.7,-7.242e-13) rot=(0,-1,0;1.5708rad)
  Reference1 = -> CoinInterieurArriere__Mirror__3_ [Face9,Face9]
  Reference2 = -> _2020_340mm [Face5,Face5]
  Suppressed = false
FEATURE [App::FeaturePython] Joint062  label="Distance057"  # Assembly joint (typed FeaturePython)
  Angle = 0
  AngleMax = 0
  AngleMin = 0
  Detach1 = false
  Detach2 = false
  Distance = 0
  Distance2 = 0
  EnableAngleMax = false
  EnableAngleMin = false
  EnableLengthMax = false
  EnableLengthMin = false
  JointType = 5 (Distance)
  LengthMax = 0
  LengthMin = 0
  Placement1 = pos=(366,1.54e-14,-150) rot=(0,0,1;0rad)
  Placement2 = pos=(-41.111,-43.9531,-38.9692) rot=(0.673149,0,0.739507;3.14159rad)
  Reference1 = -> _2020_300mm005 [Face51,Edge26]
  Reference2 = -> CoinInterieurArriere__Mirror__3_ [Face5,Face5]
  Suppressed = false
FEATURE [App::FeaturePython] Joint063  label="Distance058"  # Assembly joint (typed FeaturePython)
  Angle = 0
  AngleMax = 0
  AngleMin = 0
  Detach1 = false
  Detach2 = false
  Distance = 0
  Distance2 = 0
  EnableAngleMax = false
  EnableAngleMin = false
  EnableLengthMax = false
  EnableLengthMin = false
  JointType = 5 (Distance)
  LengthMax = 0
  LengthMin = 0
  Placement1 = pos=(356,-6.7,0) rot=(0,1,0;1.5708rad)
  Placement2 = pos=(-31.2079,-34,-38.0311) rot=(-0.613466,0.558417,0.558417;2.04107rad)
  Reference1 = -> _2020_300mm005 [Face46,Vertex98]
  Reference2 = -> CoinInterieurArriere__Mirror__3_ [Face1,Vertex6]
  Suppressed = false
FEATURE [App::FeaturePython] Joint064  label="Distance059"  # Assembly joint (typed FeaturePython)
  Angle = 0
  AngleMax = 0
  AngleMin = 0
  Detach1 = false
  Detach2 = false
  Distance = 0
  Distance2 = 0
  EnableAngleMax = false
  EnableAngleMin = false
  EnableLengthMax = false
  EnableLengthMin = false
  JointType = 5 (Distance)
  LengthMax = 0
  LengthMin = 0
  Placement1 = pos=(359.3,-10,4.547e-13) rot=(0.57735,0.57735,0.57735;4.18879rad)
  Placement2 = pos=(-32.1404,-43.9474,-28.1275) rot=(-0.046871,-0.046871,0.997801;1.573rad)
  Reference1 = -> _2020_300mm005 [Face49,Vertex100]
  Reference2 = -> CoinInterieurArriere__Mirror__3_ [Face7,Vertex19]
  Suppressed = false
FEATURE [App::FeaturePython] Joint065  label="Distance060"  # Assembly joint (typed FeaturePython)
  Angle = 0
  AngleMax = 0
  AngleMin = 0
  Detach1 = false
  Detach2 = false
  Distance = 0
  Distance2 = 0
  EnableAngleMax = false
  EnableAngleMin = false
  EnableLengthMax = false
  EnableLengthMin = false
  JointType = 5 (Distance)
  LengthMax = 0
  LengthMin = 0
  Placement1 = pos=(359.3,-10,4.547e-13) rot=(0.57735,0.57735,0.57735;4.18879rad)
  Placement2 = pos=(-32.1404,-10.0526,-28.1275) rot=(0.706717,-0.706717,0.033198;3.20796rad)
  Reference1 = -> _2020_300mm004 [Face49,Vertex99]
  Reference2 = -> CoinInterieurArriere001 [Face7,Vertex14]
  Suppressed = false
FEATURE [App::FeaturePython] Joint066  label="Distance061"  # Assembly joint (typed FeaturePython)
  Angle = 0
  AngleMax = 0
  AngleMin = 0
  Detach1 = false
  Detach2 = false
  Distance = 0
  Distance2 = 0
  EnableAngleMax = false
  EnableAngleMin = false
  EnableLengthMax = false
  EnableLengthMin = false
  JointType = 5 (Distance)
  LengthMax = 0
  LengthMin = 0
  Placement1 = pos=(376,6.7,-4.547e-13) rot=(0,-1,0;1.5708rad)
  Placement2 = pos=(-31.2079,-20,-38.0311) rot=(0.613466,-0.558417,-0.558417;4.24212rad)
  Reference1 = -> _2020_300mm004 [Face5,Vertex57]
  Reference2 = -> CoinInterieurArriere001 [Face1,Vertex6]
  Suppressed = false
FEATURE [App::FeaturePython] Joint067  label="Distance062"  # Assembly joint (typed FeaturePython)
  Angle = 0
  AngleMax = 0
  AngleMin = 0
  Detach1 = false
  Detach2 = false
  Distance = 0
  Distance2 = 0
  EnableAngleMax = false
  EnableAngleMin = false
  EnableLengthMax = false
  EnableLengthMin = false
  JointType = 5 (Distance)
  LengthMax = 0
  LengthMin = 0
  Placement1 = pos=(366,1.33e-14,-150) rot=(0,0,1;0rad)
  Placement2 = pos=(-41.111,-10.0469,-38.9692) rot=(0,-1,0;1.66468rad)
  Reference1 = -> _2020_300mm004 [Face51,Edge26]
  Reference2 = -> CoinInterieurArriere001 [Face5,Vertex15]
  Suppressed = false
FEATURE [App::Link] CoinInterieurAvant001
  LinkPlacement = pos=(70,64.583,34.9907) rot=(-0.046871,0.046871,0.997801;1.573rad)
  LinkedObject = -> <external RC-Robot-parts-export.FCStd>#Part__Feature017
  Placement = pos=(70,64.583,34.9907) rot=(-0.046871,0.046871,0.997801;1.573rad)
FEATURE [App::FeaturePython] Joint068  label="Parallel008"  # Assembly joint (typed FeaturePython)
  Angle = 0
  AngleMax = 0
  AngleMin = 0
  Detach1 = false
  Detach2 = false
  Distance = 0
  Distance2 = 0
  EnableAngleMax = false
  EnableAngleMin = false
  EnableLengthMax = false
  EnableLengthMin = false
  JointType = 6 (Parallel)
  LengthMax = 0
  LengthMin = 0
  Placement1 = pos=(276.591,-13.5902,-7.1e-15) rot=(0,1,0;1.5708rad)
  Placement2 = pos=(400.16,-3.9,-170) rot=(1,0,0;1.5708rad)
  Reference1 = -> CoinInterieurAvant001 [Face11,Face11]
  Reference2 = -> _2020_340mm002 [Face39,Vertex91]
  Suppressed = false
FEATURE [App::FeaturePython] Joint069  label="Distance063"  # Assembly joint (typed FeaturePython)
  Angle = 0
  AngleMax = 0
  AngleMin = 0
  Detach1 = false
  Detach2 = false
  Distance = 0
  Distance2 = 0
  EnableAngleMax = false
  EnableAngleMin = false
  EnableLengthMax = false
  EnableLengthMin = false
  JointType = 5 (Distance)
  LengthMax = 0
  LengthMin = 0
  Placement1 = pos=(276.591,-13.5902,-7.1e-15) rot=(0,1,0;1.5708rad)
  Placement2 = pos=(396.3,-10,6.846e-13) rot=(0.57735,0.57735,0.57735;4.18879rad)
  Reference1 = -> CoinInterieurAvant001 [Face11,Vertex40]
  Reference2 = -> _2020_340mm002 [Face49,Vertex100]
  Suppressed = false
FEATURE [App::FeaturePython] Joint070  label="Distance064"  # Assembly joint (typed FeaturePython)
  Angle = 0
  AngleMax = 0
  AngleMin = 0
  Detach1 = false
  Detach2 = false
  Distance = 0
  Distance2 = 0
  EnableAngleMax = false
  EnableAngleMin = false
  EnableLengthMax = false
  EnableLengthMin = false
  JointType = 5 (Distance)
  LengthMax = 0
  LengthMin = 0
  Placement1 = pos=(280.091,-13.3,10) rot=(0,1,0;3.14159rad)
  Placement2 = pos=(413,-6.7,6.885e-13) rot=(0,1,0;4.71239rad)
  Reference1 = -> CoinInterieurAvant001 [Face13,Face13]
  Reference2 = -> _2020_340mm002 [Face25,Vertex77]
  Suppressed = false
FEATURE [App::FeaturePython] Joint071  label="Distance065"  # Assembly joint (typed FeaturePython)
  Angle = 0
  AngleMax = 0
  AngleMin = 0
  Detach1 = false
  Detach2 = false
  Distance = 0
  Distance2 = 0
  EnableAngleMax = false
  EnableAngleMin = false
  EnableLengthMax = false
  EnableLengthMin = false
  JointType = 5 (Distance)
  LengthMax = 0
  LengthMin = 0
  Placement1 = pos=(247.472,-20,4.4977e-12) rot=(-0.57735,-0.57735,-0.57735;2.0944rad)
  Placement2 = pos=(376,6.7,-4.547e-13) rot=(0,-1,0;1.5708rad)
  Reference1 = -> CoinInterieurAvant001 [Face21,Face21]
  Reference2 = -> _2020_300mm004 [Face5,Vertex4]
  Suppressed = false
FEATURE [App::Link] CoinInterieurAvant__Mirror__2_  label="CoinInterieurAvant (Mirror #2)"
  LinkPlacement = pos=(-15,64.583,34.9907) rot=(-0.046871,0.046871,0.997801;1.573rad)
  LinkedObject = -> <external RC-Robot-parts-export.FCStd>#Part__Mirroring001
  Placement = pos=(-15,64.583,34.9907) rot=(-0.046871,0.046871,0.997801;1.573rad)
FEATURE [App::FeaturePython] Joint072  label="Parallel019"  # Assembly joint (typed FeaturePython)
  Angle = 0
  AngleMax = 0
  AngleMin = 0
  Detach1 = false
  Detach2 = false
  Distance = 0
  Distance2 = 0
  EnableAngleMax = false
  EnableAngleMin = false
  EnableLengthMax = false
  EnableLengthMin = false
  JointType = 6 (Parallel)
  LengthMax = 0
  LengthMin = 0
  Placement1 = pos=(276.591,68.5902,0) rot=(0.707107,0,-0.707107;3.14159rad)
  Placement2 = pos=(407.9,-10,170) rot=(0.57735,0.57735,0.57735;4.18879rad)
  Reference1 = -> CoinInterieurAvant__Mirror__2_ [Face11,Face11]
  Reference2 = -> _2020_340mm002 [Face29,Vertex16]
  Suppressed = false
FEATURE [App::FeaturePython] Joint073  label="Distance067"  # Assembly joint (typed FeaturePython)
  Angle = 0
  AngleMax = 0
  AngleMin = 0
  Detach1 = false
  Detach2 = false
  Distance = 0
  Distance2 = 0
  EnableAngleMax = false
  EnableAngleMin = false
  EnableLengthMax = false
  EnableLengthMin = false
  JointType = 5 (Distance)
  LengthMax = 0
  LengthMin = 0
  Placement1 = pos=(409.7,-10,-4.963e-13) rot=(0.57735,0.57735,0.57735;4.18879rad)
  Placement2 = pos=(276.591,68.5902,0) rot=(0.707107,0,-0.707107;3.14159rad)
  Reference1 = -> _2020_340mm002 [Face29,Vertex16]
  Reference2 = -> CoinInterieurAvant__Mirror__2_ [Face11,Face11]
  Suppressed = false
FEATURE [App::FeaturePython] Joint074  label="Distance068"  # Assembly joint (typed FeaturePython)
  Angle = 0
  AngleMax = 0
  AngleMin = 0
  Detach1 = false
  Detach2 = false
  Distance = 0
  Distance2 = 0
  EnableAngleMax = false
  EnableAngleMin = false
  EnableLengthMax = false
  EnableLengthMin = false
  JointType = 5 (Distance)
  LengthMax = 0
  LengthMin = 0
  Placement1 = pos=(280.091,68.3,10) rot=(0,0,-1;3.14159rad)
  Placement2 = pos=(413,-6.7,6.885e-13) rot=(0,1,0;4.71239rad)
  Reference1 = -> CoinInterieurAvant__Mirror__2_ [Face13,Face13]
  Reference2 = -> _2020_340mm002 [Face25,Vertex14]
  Suppressed = false
FEATURE [App::FeaturePython] Joint075  label="Distance069"  # Assembly joint (typed FeaturePython)
  Angle = 0
  AngleMax = 0
  AngleMin = 0
  Detach1 = false
  Detach2 = false
  Distance = 0
  Distance2 = 0
  EnableAngleMax = false
  EnableAngleMin = false
  EnableLengthMax = false
  EnableLengthMin = false
  JointType = 5 (Distance)
  LengthMax = 0
  LengthMin = 0
  Placement1 = pos=(356,6.7,0) rot=(0,1,0;1.5708rad)
  Placement2 = pos=(247.472,75,4.5119e-12) rot=(-0.57735,-0.57735,-0.57735;2.0944rad)
  Reference1 = -> _2020_300mm005 [Face26,Vertex38]
  Reference2 = -> CoinInterieurAvant__Mirror__2_ [Face21,Vertex60]
  Suppressed = false
FEATURE [App::Link] CoinInterieurArriere002
  LinkPlacement = pos=(-70,64.583,34.9907) rot=(0.706717,0.706717,-0.033198;3.07522rad)
  LinkedObject = -> <external RC-Robot-parts-export.FCStd>#Part__Feature016
  Placement = pos=(-70,64.583,34.9907) rot=(0.706717,0.706717,-0.033198;3.07522rad)
FEATURE [App::FeaturePython] Joint076  label="Parallel020"  # Assembly joint (typed FeaturePython)
  Angle = 0
  AngleMax = 0
  AngleMin = 0
  Detach1 = false
  Detach2 = false
  Distance = 0
  Distance2 = 0
  EnableAngleMax = false
  EnableAngleMin = false
  EnableLengthMax = false
  EnableLengthMin = false
  JointType = 6 (Parallel)
  LengthMax = 0
  LengthMin = 0
  Placement1 = pos=(393,-6.7,-1.13e-14) rot=(0,1,0;1.5708rad)
  Placement2 = pos=(-61.838,-13.856,-30.9237) rot=(-0.706717,-0.706717,-0.033198;3.20796rad)
  Reference1 = -> _2020_340mm001 [Face46,Face46]
  Reference2 = -> CoinInterieurArriere002 [Face18,Face18]
  Suppressed = false
FEATURE [App::FeaturePython] Joint077  label="Distance070"  # Assembly joint (typed FeaturePython)
  Angle = 0
  AngleMax = 0
  AngleMin = 0
  Detach1 = false
  Detach2 = false
  Distance = 0
  Distance2 = 0
  EnableAngleMax = false
  EnableAngleMin = false
  EnableLengthMax = false
  EnableLengthMin = false
  JointType = 5 (Distance)
  LengthMax = 0
  LengthMin = 0
  Placement1 = pos=(-61.838,-13.856,-30.9237) rot=(-0.706717,-0.706717,-0.033198;3.20796rad)
  Placement2 = pos=(393,-6.7,-1.13e-14) rot=(0,1,0;1.5708rad)
  Reference1 = -> CoinInterieurArriere002 [Face18,Face18]
  Reference2 = -> _2020_340mm001 [Face46,Vertex96]
  Suppressed = false
FEATURE [App::FeaturePython] Joint078  label="Distance071"  # Assembly joint (typed FeaturePython)
  Angle = 0
  AngleMax = 0
  AngleMin = 0
  Detach1 = false
  Detach2 = false
  Distance = 0
  Distance2 = 0
  EnableAngleMax = false
  EnableAngleMin = false
  EnableLengthMax = false
  EnableLengthMin = false
  JointType = 5 (Distance)
  LengthMax = 0
  LengthMin = 0
  Placement1 = pos=(-51.0661,-12.5475,-39.916) rot=(-0.739507,0,0.673149;3.14159rad)
  Placement2 = pos=(396.3,10,-9e-16) rot=(0.57735,0.57735,0.57735;4.18879rad)
  Reference1 = -> CoinInterieurArriere002 [Face9,Face9]
  Reference2 = -> _2020_340mm001 [Face22,Face22]
  Suppressed = false
FEATURE [App::FeaturePython] Joint079  label="Parallel021"  # Assembly joint (typed FeaturePython)
  Angle = 0
  AngleMax = 0
  AngleMin = 0
  Detach1 = false
  Detach2 = false
  Distance = 0
  Distance2 = 0
  EnableAngleMax = false
  EnableAngleMin = false
  EnableLengthMax = false
  EnableLengthMin = false
  JointType = 6 (Parallel)
  LengthMax = 0
  LengthMin = 0
  Placement1 = pos=(361.1,10,-150) rot=(-0.57735,-0.57735,-0.57735;2.0944rad)
  Placement2 = pos=(-28.4044,-10,-27.7757) rot=(-0.706717,0.706717,-0.033198;3.07522rad)
  Reference1 = -> _2020_300mm007 [Face22,Vertex72]
  Reference2 = -> CoinInterieurArriere002 [Face7,Vertex19]
  Suppressed = false
FEATURE [App::FeaturePython] Joint080  label="Distance076"  # Assembly joint (typed FeaturePython)
  Angle = 0
  AngleMax = 0
  AngleMin = 0
  Detach1 = false
  Detach2 = false
  Distance = 0
  Distance2 = 0
  EnableAngleMax = false
  EnableAngleMin = false
  EnableLengthMax = false
  EnableLengthMin = false
  JointType = 5 (Distance)
  LengthMax = 0
  LengthMin = 0
  Placement1 = pos=(366,1.42e-14,-150) rot=(0,0,1;0rad)
  Placement2 = pos=(-41.111,-10.0469,-38.9692) rot=(0,-1,0;1.66468rad)
  Reference1 = -> _2020_300mm007 [Face51,Edge38]
  Reference2 = -> CoinInterieurArriere002 [Face5,Face5]
  Suppressed = false
FEATURE [App::FeaturePython] Joint081  label="Distance077"  # Assembly joint (typed FeaturePython)
  Angle = 0
  AngleMax = 0
  AngleMin = 0
  Detach1 = false
  Detach2 = false
  Distance = 0
  Distance2 = 0
  EnableAngleMax = false
  EnableAngleMin = false
  EnableLengthMax = false
  EnableLengthMin = false
  JointType = 5 (Distance)
  LengthMax = 0
  LengthMin = 0
  Placement1 = pos=(359.3,10,-2.84e-14) rot=(-0.57735,-0.57735,-0.57735;2.0944rad)
  Placement2 = pos=(-32.1404,-10.0526,-28.1275) rot=(-0.706717,0.706717,-0.033198;3.07522rad)
  Reference1 = -> _2020_300mm007 [Face22,Vertex74]
  Reference2 = -> CoinInterieurArriere002 [Face7,Face7]
  Suppressed = false
FEATURE [App::FeaturePython] Joint082  label="Distance078"  # Assembly joint (typed FeaturePython)
  Angle = 0
  AngleMax = 0
  AngleMin = 0
  Detach1 = false
  Detach2 = false
  Distance = 0
  Distance2 = 0
  EnableAngleMax = false
  EnableAngleMin = false
  EnableLengthMax = false
  EnableLengthMin = false
  JointType = 5 (Distance)
  LengthMax = 0
  LengthMin = 0
  Placement1 = pos=(356,-6.7,-2.84e-14) rot=(0,1,0;1.5708rad)
  Placement2 = pos=(-31.2079,-20,-38.0311) rot=(-0.613466,0.558417,0.558417;2.04107rad)
  Reference1 = -> _2020_300mm007 [Face46,Vertex96]
  Reference2 = -> CoinInterieurArriere002 [Face1,Vertex1]
  Suppressed = false
FEATURE [App::FeaturePython] Joint083  label="Distance079"  # Assembly joint (typed FeaturePython)
  Angle = 0
  AngleMax = 0
  AngleMin = 0
  Detach1 = false
  Detach2 = false
  Distance = 0
  Distance2 = 0
  EnableAngleMax = false
  EnableAngleMin = false
  EnableLengthMax = false
  EnableLengthMin = false
  JointType = 5 (Distance)
  LengthMax = 0
  LengthMin = 0
  Placement1 = pos=(356,6.7,0) rot=(0,1,0;1.5708rad)
  Placement2 = pos=(247.472,75,4.5119e-12) rot=(-0.57735,-0.57735,-0.57735;2.0944rad)
  Reference1 = -> _2020_300mm007 [Face26,Vertex38]
  Reference2 = -> CoinInterieurAvant__Mirror__2_ [Face21,Face21]
  Suppressed = false
FEATURE [App::Link] CoinInterieurArriere__Mirror__3_001  label="CoinInterieurArriere (Mirror #3)001"
  LinkPlacement = pos=(124,64.583,34.9907) rot=(0.706717,0.706717,-0.033198;3.07522rad)
  LinkedObject = -> <external RC-Robot-parts-export.FCStd>#Part__Mirroring002
  Placement = pos=(124,64.583,34.9907) rot=(0.706717,0.706717,-0.033198;3.07522rad)
FEATURE [App::FeaturePython] Joint084  label="Parallel022"  # Assembly joint (typed FeaturePython)
  Angle = 0
  AngleMax = 0
  AngleMin = 0
  Detach1 = false
  Detach2 = false
  Distance = 0
  Distance2 = 0
  EnableAngleMax = false
  EnableAngleMin = false
  EnableLengthMax = false
  EnableLengthMin = false
  JointType = 6 (Parallel)
  LengthMax = 0
  LengthMin = 0
  Placement1 = pos=(-61.838,-40.144,-30.9237) rot=(0.046871,-0.046871,-0.997801;1.573rad)
  Placement2 = pos=(393,-8.5,-170) rot=(0,1,0;1.5708rad)
  Reference1 = -> CoinInterieurArriere__Mirror__3_001 [Face18,Face18]
  Reference2 = -> _2020_340mm001 [Face46,Vertex98]
  Suppressed = false
FEATURE [App::FeaturePython] Joint085  label="Distance080"  # Assembly joint (typed FeaturePython)
  Angle = 0
  AngleMax = 0
  AngleMin = 0
  Detach1 = false
  Detach2 = false
  Distance = 0
  Distance2 = 0
  EnableAngleMax = false
  EnableAngleMin = false
  EnableLengthMax = false
  EnableLengthMin = false
  JointType = 5 (Distance)
  LengthMax = 0
  LengthMin = 0
  Placement1 = pos=(393,-6.7,-1.13e-14) rot=(0,1,0;1.5708rad)
  Placement2 = pos=(-61.838,-40.144,-30.9237) rot=(0.046871,-0.046871,-0.997801;1.573rad)
  Reference1 = -> _2020_340mm001 [Face46,Vertex98]
  Reference2 = -> CoinInterieurArriere__Mirror__3_001 [Face18,Face18]
  Suppressed = false
FEATURE [App::FeaturePython] Joint086  label="Distance081"  # Assembly joint (typed FeaturePython)
  Angle = 0
  AngleMax = 0
  AngleMin = 0
  Detach1 = false
  Detach2 = false
  Distance = 0
  Distance2 = 0
  EnableAngleMax = false
  EnableAngleMin = false
  EnableLengthMax = false
  EnableLengthMin = false
  JointType = 5 (Distance)
  LengthMax = 0
  LengthMin = 0
  Placement1 = pos=(-51.0661,-41.4525,-39.916) rot=(0,1,0;1.47692rad)
  Placement2 = pos=(396.3,10,-9e-16) rot=(0.57735,0.57735,0.57735;4.18879rad)
  Reference1 = -> CoinInterieurArriere__Mirror__3_001 [Face9,Face9]
  Reference2 = -> _2020_340mm001 [Face22,Vertex74]
  Suppressed = false
FEATURE [App::FeaturePython] Joint087  label="Parallel023"  # Assembly joint (typed FeaturePython)
  Angle = 0
  AngleMax = 0
  AngleMin = 0
  Detach1 = false
  Detach2 = false
  Distance = 0
  Distance2 = 0
  EnableAngleMax = false
  EnableAngleMin = false
  EnableLengthMax = false
  EnableLengthMin = false
  JointType = 6 (Parallel)
  LengthMax = 0
  LengthMin = 0
  Placement1 = pos=(-32.1404,-43.9474,-28.1275) rot=(-0.046871,-0.046871,0.997801;1.573rad)
  Placement2 = pos=(361.1,10,-150) rot=(-0.57735,-0.57735,-0.57735;2.0944rad)
  Reference1 = -> CoinInterieurArriere__Mirror__3_001 [Face7,Face7]
  Reference2 = -> _2020_300mm006 [Face22,Vertex72]
  Suppressed = false
FEATURE [App::FeaturePython] Joint088  label="Distance082"  # Assembly joint (typed FeaturePython)
  Angle = 0
  AngleMax = 0
  AngleMin = 0
  Detach1 = false
  Detach2 = false
  Distance = 0
  Distance2 = 0
  EnableAngleMax = false
  EnableAngleMin = false
  EnableLengthMax = false
  EnableLengthMin = false
  JointType = 5 (Distance)
  LengthMax = 0
  LengthMin = 0
  Placement1 = pos=(366,0,-150) rot=(0,0,1;0rad)
  Placement2 = pos=(-41.111,-43.9531,-38.9692) rot=(0.673149,0,0.739507;3.14159rad)
  Reference1 = -> _2020_300mm006 [Face51,Edge26]
  Reference2 = -> CoinInterieurArriere__Mirror__3_001 [Face5,Face5]
  Suppressed = false
FEATURE [App::FeaturePython] Joint089  label="Distance083"  # Assembly joint (typed FeaturePython)
  Angle = 0
  AngleMax = 0
  AngleMin = 0
  Detach1 = false
  Detach2 = false
  Distance = 0
  Distance2 = 0
  EnableAngleMax = false
  EnableAngleMin = false
  EnableLengthMax = false
  EnableLengthMin = false
  JointType = 5 (Distance)
  LengthMax = 0
  LengthMin = 0
  Placement1 = pos=(359.3,10,0) rot=(-0.57735,-0.57735,-0.57735;2.0944rad)
  Placement2 = pos=(-32.1404,-43.9474,-28.1275) rot=(-0.046871,-0.046871,0.997801;1.573rad)
  Reference1 = -> _2020_300mm006 [Face22,Vertex72]
  Reference2 = -> CoinInterieurArriere__Mirror__3_001 [Face7,Face7]
  Suppressed = false
FEATURE [App::FeaturePython] Joint090  label="Distance084"  # Assembly joint (typed FeaturePython)
  Angle = 0
  AngleMax = 0
  AngleMin = 0
  Detach1 = false
  Detach2 = false
  Distance = 0
  Distance2 = 0
  EnableAngleMax = false
  EnableAngleMin = false
  EnableLengthMax = false
  EnableLengthMin = false
  JointType = 5 (Distance)
  LengthMax = 0
  LengthMin = 0
  Placement1 = pos=(376,-6.7,5.116e-13) rot=(0,1,0;4.71239rad)
  Placement2 = pos=(-31.2079,-34,-38.0311) rot=(-0.613466,0.558417,0.558417;2.04107rad)
  Reference1 = -> _2020_300mm006 [Face25,Vertex75]
  Reference2 = -> CoinInterieurArriere__Mirror__3_001 [Face1,Vertex1]
  Suppressed = false
FEATURE [App::FeaturePython] Joint091  label="Distance085"  # Assembly joint (typed FeaturePython)
  Angle = 0
  AngleMax = 0
  AngleMin = 0
  Detach1 = false
  Detach2 = false
  Distance = 0
  Distance2 = 0
  EnableAngleMax = false
  EnableAngleMin = false
  EnableLengthMax = false
  EnableLengthMin = false
  JointType = 5 (Distance)
  LengthMax = 0
  LengthMin = 0
  Placement1 = pos=(376,6.7,-4.263e-13) rot=(0,1,0;4.71239rad)
  Placement2 = pos=(247.472,-20,4.4977e-12) rot=(-0.57735,-0.57735,-0.57735;2.0944rad)
  Reference1 = -> _2020_300mm006 [Face5,Vertex3]
  Reference2 = -> CoinInterieurAvant001 [Face21,Vertex62]
  Suppressed = false
FEATURE [App::Link] GardeBoue
  LinkPlacement = pos=(180,68.0254,34.3367) rot=(-0.046871,0.046871,0.997801;1.573rad)
  LinkedObject = -> <external RC-Robot-parts-export.FCStd>#Part__Feature009
  Placement = pos=(180,68.0254,34.3367) rot=(-0.046871,0.046871,0.997801;1.573rad)
FEATURE [App::Link] GardeBoue001
  LinkPlacement = pos=(-90,68.0254,34.3367) rot=(-0.046871,0.046871,0.997801;1.573rad)
  LinkedObject = -> <external RC-Robot-parts-export.FCStd>#Part__Feature009
  Placement = pos=(-90,68.0254,34.3367) rot=(-0.046871,0.046871,0.997801;1.573rad)
FEATURE [App::FeaturePython] Joint092  label="Parallel024"  # Assembly joint (typed FeaturePython)
  Angle = 0
  AngleMax = 0
  AngleMin = 0
  Detach1 = false
  Detach2 = false
  Distance = 0
  Distance2 = 0
  EnableAngleMax = false
  EnableAngleMin = false
  EnableLengthMax = false
  EnableLengthMin = false
  JointType = 6 (Parallel)
  LengthMax = 0
  LengthMin = 0
  Placement1 = pos=(374.5,-10,-150) rot=(-0.57735,-0.57735,-0.57735;2.0944rad)
  Placement2 = pos=(57.6082,8,39.7655) rot=(0,1,0;0.09388rad)
  Reference1 = -> _2020_300mm003 [Face29,Vertex79]
  Reference2 = -> GardeBoue001 [Face3,Vertex24]
  Suppressed = false
FEATURE [App::FeaturePython] Joint093  label="Distance086"  # Assembly joint (typed FeaturePython)
  Angle = 0
  AngleMax = 0
  AngleMin = 0
  Detach1 = false
  Detach2 = false
  Distance = 0
  Distance2 = 0
  EnableAngleMax = false
  EnableAngleMin = false
  EnableLengthMax = false
  EnableLengthMin = false
  JointType = 5 (Distance)
  LengthMax = 0
  LengthMin = 0
  Placement1 = pos=(66.2907,2.84e-14,23.2633) rot=(0.57735,-0.57735,0.57735;2.0944rad)
  Placement2 = pos=(356,6.7,0) rot=(0,1,0;1.5708rad)
  Reference1 = -> GardeBoue001 [Face1,Vertex1]
  Reference2 = -> _2020_300mm007 [Face26,Vertex78]
  Suppressed = false
FEATURE [App::FeaturePython] Joint094  label="Distance087"  # Assembly joint (typed FeaturePython)
  Angle = 0
  AngleMax = 0
  AngleMin = 0
  Detach1 = false
  Detach2 = false
  Distance = 0
  Distance2 = 0
  EnableAngleMax = false
  EnableAngleMin = false
  EnableLengthMax = false
  EnableLengthMin = false
  JointType = 5 (Distance)
  LengthMax = 0
  LengthMin = 0
  Placement1 = pos=(376,6.7,-4.547e-13) rot=(0,1,0;4.71239rad)
  Placement2 = pos=(66.2907,90,23.2633) rot=(0,-0.707107,-0.707107;3.14159rad)
  Reference1 = -> _2020_300mm003 [Face5,Vertex57]
  Reference2 = -> GardeBoue001 [Face20,Face20]
  Suppressed = false
FEATURE [App::FeaturePython] Joint095  label="Distance088"  # Assembly joint (typed FeaturePython)
  Angle = 0
  AngleMax = 0
  AngleMin = 0
  Detach1 = false
  Detach2 = false
  Distance = 0
  Distance2 = 0
  EnableAngleMax = false
  EnableAngleMin = false
  EnableLengthMax = false
  EnableLengthMin = false
  JointType = 5 (Distance)
  LengthMax = 0
  LengthMin = 0
  Placement1 = pos=(58.8689,45,39.6468) rot=(0,1,0;0.09388rad)
  Placement2 = pos=(372.7,-10,-4.547e-13) rot=(-0.57735,-0.57735,-0.57735;2.0944rad)
  Reference1 = -> GardeBoue001 [Face3,Vertex24]
  Reference2 = -> _2020_300mm003 [Face29,Vertex81]
  Suppressed = false
FEATURE [App::FeaturePython] Joint096  label="Parallel025"  # Assembly joint (typed FeaturePython)
  Angle = 0
  AngleMax = 0
  AngleMin = 0
  Detach1 = false
  Detach2 = false
  Distance = 0
  Distance2 = 0
  EnableAngleMax = false
  EnableAngleMin = false
  EnableLengthMax = false
  EnableLengthMin = false
  JointType = 6 (Parallel)
  LengthMax = 0
  LengthMin = 0
  Placement1 = pos=(57.6082,82,39.7655) rot=(0,1,0;0.09388rad)
  Placement2 = pos=(359.3,10,-2.84e-14) rot=(-0.57735,-0.57735,-0.57735;2.0944rad)
  Reference1 = -> GardeBoue [Face3,Vertex25]
  Reference2 = -> _2020_300mm001 [Face22,Face22]
  Suppressed = false
FEATURE [App::FeaturePython] Joint097  label="Distance089"  # Assembly joint (typed FeaturePython)
  Angle = 0
  AngleMax = 0
  AngleMin = 0
  Detach1 = false
  Detach2 = false
  Distance = 0
  Distance2 = 0
  EnableAngleMax = false
  EnableAngleMin = false
  EnableLengthMax = false
  EnableLengthMin = false
  JointType = 5 (Distance)
  LengthMax = 0
  LengthMin = 0
  Placement1 = pos=(66.2907,90,23.2633) rot=(0,-0.707107,-0.707107;3.14159rad)
  Placement2 = pos=(376,-6.7,5.116e-13) rot=(0,1,0;4.71239rad)
  Reference1 = -> GardeBoue [Face20,Vertex46]
  Reference2 = -> _2020_300mm006 [Face25,Vertex77]
  Suppressed = false
FEATURE [App::FeaturePython] Joint098  label="Distance090"  # Assembly joint (typed FeaturePython)
  Angle = 0
  AngleMax = 0
  AngleMin = 0
  Detach1 = false
  Detach2 = false
  Distance = 0
  Distance2 = 0
  EnableAngleMax = false
  EnableAngleMin = false
  EnableLengthMax = false
  EnableLengthMin = false
  JointType = 5 (Distance)
  LengthMax = 0
  LengthMin = 0
  Placement1 = pos=(66.2907,0,23.2633) rot=(0.57735,-0.57735,0.57735;2.0944rad)
  Placement2 = pos=(356,-6.7,0) rot=(0,1,0;1.5708rad)
  Reference1 = -> GardeBoue [Face1,Vertex1]
  Reference2 = -> _2020_300mm001 [Face46,Vertex27]
  Suppressed = false
FEATURE [App::FeaturePython] Joint099  label="Distance091"  # Assembly joint (typed FeaturePython)
  Angle = 0
  AngleMax = 0
  AngleMin = 0
  Detach1 = false
  Detach2 = false
  Distance = 0
  Distance2 = 0
  EnableAngleMax = false
  EnableAngleMin = false
  EnableLengthMax = false
  EnableLengthMin = false
  JointType = 5 (Distance)
  LengthMax = 0
  LengthMin = 0
  Placement1 = pos=(58.8689,45,39.6468) rot=(0,1,0;0.09388rad)
  Placement2 = pos=(359.3,10,-2.84e-14) rot=(-0.57735,-0.57735,-0.57735;2.0944rad)
  Reference1 = -> GardeBoue [Face3,Vertex2]
  Reference2 = -> _2020_300mm001 [Face22,Vertex40]
  Suppressed = false
FEATURE [App::FeaturePython] Joint100  label="Distance092"  # Assembly joint (typed FeaturePython)
  Angle = 0
  AngleMax = 0
  AngleMin = 0
  Detach1 = false
  Detach2 = false
  Distance = 105
  Distance2 = 0
  EnableAngleMax = false
  EnableAngleMin = false
  EnableLengthMax = false
  EnableLengthMin = false
  JointType = 5 (Distance)
  LengthMax = 0
  LengthMin = 0
  Placement1 = pos=(409.7,10,-4.3e-15) rot=(0.57735,0.57735,0.57735;4.18879rad)
  Placement2 = pos=(50.924,45,40.3949) rot=(-0.57735,-0.57735,0.57735;4.18879rad)
  Reference1 = -> _2020_340mm001 [Face2,Vertex2]
  Reference2 = -> GardeBoue001 [Edge21,Edge21]
  Suppressed = false
FEATURE [App::FeaturePython] Joint101  label="Distance093"  # Assembly joint (typed FeaturePython)
  Angle = 0
  AngleMax = 0
  AngleMin = 0
  Detach1 = false
  Detach2 = false
  Distance = 105
  Distance2 = 0
  EnableAngleMax = false
  EnableAngleMin = false
  EnableLengthMax = false
  EnableLengthMin = false
  JointType = 5 (Distance)
  LengthMax = 0
  LengthMin = 0
  Placement1 = pos=(409.7,10,-4.3e-15) rot=(0.57735,0.57735,0.57735;4.18879rad)
  Placement2 = pos=(50.924,45,40.3949) rot=(-0.57735,-0.57735,0.57735;4.18879rad)
  Reference1 = -> _2020_340mm001 [Face2,Vertex54]
  Reference2 = -> GardeBoue [Edge21,Edge21]
  Suppressed = false
FEATURE [App::Link] motor_mounted  label="motor-mounted"
  LinkPlacement = pos=(100,164.143,25.6165) rot=(0,0.046923,0.998899;3.14159rad)
  LinkedObject = -> <external RC-Robot-parts-export.FCStd>#Part
  Placement = pos=(100,164.143,25.6165) rot=(0,0.046923,0.998899;3.14159rad)
FEATURE [App::Link] motor_mounted001  label="motor-mounted001"
  LinkPlacement = pos=(-100,164.143,25.6165) rot=(1,0,0;3.04771rad)
  LinkedObject = -> <external RC-Robot-parts-export.FCStd>#Part
  Placement = pos=(-100,164.143,25.6165) rot=(1,0,0;3.04771rad)
FEATURE [App::FeaturePython] Joint102  label="Parallel026"  # Assembly joint (typed FeaturePython)
  Angle = 0
  AngleMax = 0
  AngleMin = 0
  Detach1 = false
  Detach2 = false
  Distance = 0
  Distance2 = 0
  EnableAngleMax = false
  EnableAngleMin = false
  EnableLengthMax = false
  EnableLengthMin = false
  JointType = 6 (Parallel)
  LengthMax = 0
  LengthMin = 0
  Placement2 = pos=(361.1,-10,-150) rot=(-0.57735,-0.57735,-0.57735;2.0944rad)
  Reference2 = -> _2020_300mm006 [Face49,Vertex99]
  Suppressed = false
FEATURE [App::FeaturePython] Joint103  label="Distance094"  # Assembly joint (typed FeaturePython)
  Angle = 0
  AngleMax = 0
  AngleMin = 0
  Detach1 = false
  Detach2 = false
  Distance = 0
  Distance2 = 0
  EnableAngleMax = false
  EnableAngleMin = false
  EnableLengthMax = false
  EnableLengthMin = false
  JointType = 5 (Distance)
  LengthMax = 0
  LengthMin = 0
  Placement2 = pos=(376,-6.7,5.116e-13) rot=(0,1,0;4.71239rad)
  Reference2 = -> _2020_300mm006 [Face25,Vertex77]
  Suppressed = false
FEATURE [App::FeaturePython] Joint104  label="Distance095"  # Assembly joint (typed FeaturePython)
  Angle = 0
  AngleMax = 0
  AngleMin = 0
  Detach1 = false
  Detach2 = false
  Distance = 0
  Distance2 = 0
  EnableAngleMax = false
  EnableAngleMin = false
  EnableLengthMax = false
  EnableLengthMin = false
  JointType = 5 (Distance)
  LengthMax = 0
  LengthMin = 0
  Placement2 = pos=(359.3,10,0) rot=(-0.57735,-0.57735,-0.57735;2.0944rad)
  Reference2 = -> _2020_300mm006 [Face22,Vertex72]
  Suppressed = false
FEATURE [App::FeaturePython] Joint105  label="Distance097"  # Assembly joint (typed FeaturePython)
  Angle = 0
  AngleMax = 0
  AngleMin = 0
  Detach1 = false
  Detach2 = false
  Distance = 0
  Distance2 = 0
  EnableAngleMax = false
  EnableAngleMin = false
  EnableLengthMax = false
  EnableLengthMin = false
  JointType = 5 (Distance)
  LengthMax = 0
  LengthMin = 0
  Placement2 = pos=(359.3,-10,4.547e-13) rot=(0.57735,0.57735,0.57735;4.18879rad)
  Reference2 = -> _2020_300mm004 [Face49,Vertex100]
  Suppressed = false
FEATURE [App::FeaturePython] Joint106  label="Distance098"  # Assembly joint (typed FeaturePython)
  Angle = 0
  AngleMax = 0
  AngleMin = 0
  Detach1 = false
  Detach2 = false
  Distance = 0
  Distance2 = 0
  EnableAngleMax = false
  EnableAngleMin = false
  EnableLengthMax = false
  EnableLengthMin = false
  JointType = 5 (Distance)
  LengthMax = 0
  LengthMin = 0
  Placement2 = pos=(372.7,-10,-4.547e-13) rot=(-0.57735,-0.57735,-0.57735;2.0944rad)
  Reference2 = -> _2020_300mm007 [Face29,Face29]
  Suppressed = false
FEATURE [App::FeaturePython] Joint107  label="Distance099"  # Assembly joint (typed FeaturePython)
  Angle = 0
  AngleMax = 0
  AngleMin = 0
  Detach1 = false
  Detach2 = false
  Distance = 0
  Distance2 = 0
  EnableAngleMax = false
  EnableAngleMin = false
  EnableLengthMax = false
  EnableLengthMin = false
  JointType = 5 (Distance)
  LengthMax = 0
  LengthMin = 0
  Placement2 = pos=(356,-6.7,-2.84e-14) rot=(0,1,0;1.5708rad)
  Reference2 = -> _2020_300mm007 [Face46,Face46]
  Suppressed = false
FEATURE [App::FeaturePython] Joint108  label="Distance100"  # Assembly joint (typed FeaturePython)
  Angle = 0
  AngleMax = 0
  AngleMin = 0
  Detach1 = false
  Detach2 = false
  Distance = 0
  Distance2 = 0
  EnableAngleMax = false
  EnableAngleMin = false
  EnableLengthMax = false
  EnableLengthMin = false
  JointType = 5 (Distance)
  LengthMax = 0
  LengthMin = 0
  Placement2 = pos=(359.3,-10,4.547e-13) rot=(0.57735,0.57735,0.57735;4.18879rad)
  Reference2 = -> _2020_300mm005 [Face49,Vertex99]
  Suppressed = false
FEATURE [App::Link] EnsembleRoue
  LinkPlacement = pos=(-145.4,64.583,34.9907) rot=(-1,0,0;0.09388rad)
  LinkedObject = -> <external actuators-parts/wheel.FCStd>#Part001
  Placement = pos=(-145.4,64.583,34.9907) rot=(-1,0,0;0.09388rad)
FEATURE [App::Link] EnsembleRoue001
  LinkPlacement = pos=(145.4,64.583,34.9907) rot=(0,0.998899,-0.046923;3.14159rad)
  LinkedObject = -> <external actuators-parts/wheel.FCStd>#Part001
  Placement = pos=(145.4,64.583,34.9907) rot=(0,0.998899,-0.046923;3.14159rad)
FEATURE [App::FeaturePython] Joint109  label="Fixed008"  # Assembly joint (typed FeaturePython)
  Angle = 0
  AngleMax = 0
  AngleMin = 0
  Detach1 = false
  Detach2 = false
  Distance = 0
  Distance2 = 0
  EnableAngleMax = false
  EnableAngleMin = false
  EnableLengthMax = false
  EnableLengthMin = false
  JointType = 0 (Fixed)
  LengthMax = 0
  LengthMin = 0
  Offset2 = pos=(0,0,-10) rot=(0,0,1;0rad)
  Placement1 = pos=(40,-4.41e-14,1.74e-14) rot=(0.57735,0.57735,0.57735;2.0944rad)
  Placement2 = pos=(-5.4,5.6e-15,2.19e-14) rot=(-0.57735,-0.57735,0.57735;2.0944rad)
  Reference1 = -> EnsembleRoue001 [Body006.Edge23,Body006.Edge23]
  Suppressed = false
FEATURE [App::FeaturePython] Joint110  label="Fixed009"  # Assembly joint (typed FeaturePython)
  Angle = 0
  AngleMax = 0
  AngleMin = 0
  Detach1 = false
  Detach2 = false
  Distance = 0
  Distance2 = 0
  EnableAngleMax = false
  EnableAngleMin = false
  EnableLengthMax = false
  EnableLengthMin = false
  JointType = 0 (Fixed)
  LengthMax = 0
  LengthMin = 0
  Offset2 = pos=(0,0,-10) rot=(0,0,1;0rad)
  Placement1 = pos=(40,-4.41e-14,1.74e-14) rot=(0.57735,0.57735,0.57735;2.0944rad)
  Placement2 = pos=(-5.4,5.6e-15,2.19e-14) rot=(-0.57735,-0.57735,0.57735;2.0944rad)
  Reference1 = -> EnsembleRoue [Body006.Edge23,Body006.Edge23]
  Suppressed = false
FEATURE [App::Link] SupportAxeRoulement
  LinkPlacement = pos=(180,64.5822,34.9908) rot=(-0.04687,0.04687,0.997801;1.573rad)
  LinkedObject = -> <external RC-Robot-parts-export.FCStd>#Part__Feature004
  Placement = pos=(180,64.5822,34.9908) rot=(-0.04687,0.04687,0.997801;1.573rad)
FEATURE [App::Link] SupportAxeRoulement001
  LinkPlacement = pos=(-180,64.583,34.9908) rot=(0.706717,0.706717,-0.033197;3.07522rad)
  LinkedObject = -> <external RC-Robot-parts-export.FCStd>#Part__Feature004
  Placement = pos=(-180,64.583,34.9908) rot=(0.706717,0.706717,-0.033197;3.07522rad)
FEATURE [App::FeaturePython] Joint111  label="Distance101"  # Assembly joint (typed FeaturePython)
  Angle = 0
  AngleMax = 0
  AngleMin = 0
  Detach1 = false
  Detach2 = false
  Distance = 0
  Distance2 = 0
  EnableAngleMax = false
  EnableAngleMin = false
  EnableLengthMax = false
  EnableLengthMin = false
  JointType = 5 (Distance)
  LengthMax = 0
  LengthMin = 0
  Placement1 = pos=(372.7,10,-2.84e-14) rot=(-0.57735,-0.57735,-0.57735;2.0944rad)
  Reference1 = -> _2020_300mm001 [Face2,Vertex2]
  Suppressed = false
FEATURE [App::FeaturePython] Joint112  label="Distance102"  # Assembly joint (typed FeaturePython)
  Angle = 0
  AngleMax = 0
  AngleMin = 0
  Detach1 = false
  Detach2 = false
  Distance = 0
  Distance2 = 0
  EnableAngleMax = false
  EnableAngleMin = false
  EnableLengthMax = false
  EnableLengthMin = false
  JointType = 5 (Distance)
  LengthMax = 0
  LengthMin = 0
  Placement2 = pos=(376,-6.7,4.547e-13) rot=(0,-1,0;1.5708rad)
  Reference2 = -> _2020_300mm001 [Face25,Vertex14]
  Suppressed = false
FEATURE [App::FeaturePython] Joint113  label="Distance103"  # Assembly joint (typed FeaturePython)
  Angle = 0
  AngleMax = 0
  AngleMin = 0
  Detach1 = false
  Detach2 = false
  Distance = 0
  Distance2 = 0
  EnableAngleMax = false
  EnableAngleMin = false
  EnableLengthMax = false
  EnableLengthMin = false
  JointType = 5 (Distance)
  LengthMax = 0
  LengthMin = 0
  Placement2 = pos=(372.7,-10,-4.547e-13) rot=(0.57735,0.57735,0.57735;4.18879rad)
  Reference2 = -> _2020_300mm [Face29,Vertex81]
  Suppressed = false
FEATURE [App::FeaturePython] Joint114  label="Parallel010"  # Assembly joint (typed FeaturePython)
  Angle = 0
  AngleMax = 0
  AngleMin = 0
  Detach1 = false
  Detach2 = false
  Distance = 0
  Distance2 = 0
  EnableAngleMax = false
  EnableAngleMin = false
  EnableLengthMax = false
  EnableLengthMin = false
  JointType = 6 (Parallel)
  LengthMax = 0
  LengthMin = 0
  Placement2 = pos=(361.1,-10,-150) rot=(-0.57735,-0.57735,-0.57735;2.0944rad)
  Reference2 = -> _2020_300mm003 [Face49,Vertex99]
  Suppressed = false
FEATURE [App::FeaturePython] Joint115  label="Distance104"  # Assembly joint (typed FeaturePython)
  Angle = 0
  AngleMax = 0
  AngleMin = 0
  Detach1 = false
  Detach2 = false
  Distance = 0
  Distance2 = 0
  EnableAngleMax = false
  EnableAngleMin = false
  EnableLengthMax = false
  EnableLengthMin = false
  JointType = 5 (Distance)
  LengthMax = 0
  LengthMin = 0
  Placement1 = pos=(-49.1588,-20,29.5047) rot=(-0.57735,-0.57735,-0.57735;2.0944rad)
  Placement2 = pos=(356,-6.7,0) rot=(0,1,0;1.5708rad)
  Reference1 = -> CoinLateralHG [Face11,Face11]
  Reference2 = -> _2020_300mm003 [Face46,Vertex96]
  Suppressed = false
FEATURE [App::FeaturePython] Joint116  label="Distance105"  # Assembly joint (typed FeaturePython)
  Angle = 0
  AngleMax = 0
  AngleMin = 0
  Detach1 = false
  Detach2 = false
  Distance = 0
  Distance2 = 0
  EnableAngleMax = false
  EnableAngleMin = false
  EnableLengthMax = false
  EnableLengthMin = false
  JointType = 5 (Distance)
  LengthMax = 0
  LengthMin = 0
  Placement2 = pos=(359.3,10,0) rot=(-0.57735,-0.57735,-0.57735;2.0944rad)
  Reference2 = -> _2020_300mm003 [Face22,Vertex74]
  Suppressed = false
FEATURE [App::FeaturePython] Joint117  label="Distance106"  # Assembly joint (typed FeaturePython)
  Angle = 0
  AngleMax = 0
  AngleMin = 0
  Detach1 = false
  Detach2 = false
  Distance = 0
  Distance2 = 0
  EnableAngleMax = false
  EnableAngleMin = false
  EnableLengthMax = false
  EnableLengthMin = false
  JointType = 5 (Distance)
  LengthMax = 0
  LengthMin = 0
  Placement2 = pos=(359.3,-10,4.547e-13) rot=(0.57735,0.57735,0.57735;4.18879rad)
  Reference2 = -> _2020_300mm002 [Face49,Vertex99]
  Suppressed = false
FEATURE [App::FeaturePython] Joint118  label="Distance107"  # Assembly joint (typed FeaturePython)
  Angle = 0
  AngleMax = 0
  AngleMin = 0
  Detach1 = false
  Detach2 = false
  Distance = 0
  Distance2 = 0
  EnableAngleMax = false
  EnableAngleMin = false
  EnableLengthMax = false
  EnableLengthMin = false
  JointType = 5 (Distance)
  LengthMax = 0
  LengthMin = 0
  Placement2 = pos=(356,6.7,-2.84e-14) rot=(0,1,0;1.5708rad)
  Reference2 = -> _2020_300mm003 [Face26,Vertex76]
  Suppressed = false
FEATURE [App::Link] free_wheel_support  label="free-wheel-support"
  LinkPlacement = pos=(-133.5,339.019,-0.893384) rot=(-0.046871,0.046871,0.997801;1.573rad)
  LinkedObject = -> <external mecanical-parts/free-wheel-support.FCStd>#Body
  Placement = pos=(-133.5,339.019,-0.893384) rot=(-0.046871,0.046871,0.997801;1.573rad)
FEATURE [App::Link] free_wheel_support001  label="free-wheel-support001"
  LinkPlacement = pos=(133.5,339.019,-0.893384) rot=(-0.046871,0.046871,0.997801;1.573rad)
  LinkedObject = -> <external mecanical-parts/free-wheel-support.FCStd>#Body
  Placement = pos=(133.5,339.019,-0.893384) rot=(-0.046871,0.046871,0.997801;1.573rad)
FEATURE [App::FeaturePython] Joint119  label="Parallel027"  # Assembly joint (typed FeaturePython)
  Angle = 0
  AngleMax = 0
  AngleMin = 0
  Detach1 = false
  Detach2 = false
  Distance = 0
  Distance2 = 0
  EnableAngleMax = false
  EnableAngleMin = false
  EnableLengthMax = false
  EnableLengthMin = false
  JointType = 6 (Parallel)
  LengthMax = 0
  LengthMin = 0
  Placement1 = pos=(9.82583,0,0) rot=(0,0,1;0rad)
  Placement2 = pos=(393,-8.5,170) rot=(0,1,0;1.5708rad)
  Reference1 = -> free_wheel_support [Face7,Face7]
  Reference2 = -> _2020_340mm002 [Face46,Vertex27]
  Suppressed = false
FEATURE [App::FeaturePython] Joint120  label="Distance108"  # Assembly joint (typed FeaturePython)
  Angle = 0
  AngleMax = 0
  AngleMin = 0
  Detach1 = false
  Detach2 = false
  Distance = 0
  Distance2 = 0
  EnableAngleMax = false
  EnableAngleMin = false
  EnableLengthMax = false
  EnableLengthMin = false
  JointType = 5 (Distance)
  LengthMax = 0
  LengthMin = 0
  Placement1 = pos=(9.82583,0,0) rot=(0,0,1;0rad)
  Placement2 = pos=(393,-6.7,9.11e-14) rot=(0,1,0;1.5708rad)
  Reference1 = -> free_wheel_support [Face7,Face7]
  Reference2 = -> _2020_340mm002 [Face46,Vertex27]
  Suppressed = false
FEATURE [App::FeaturePython] Joint121  label="Distance110"  # Assembly joint (typed FeaturePython)
  Angle = 0
  AngleMax = 0
  AngleMin = 0
  Detach1 = false
  Detach2 = false
  Distance = 0
  Distance2 = 0
  EnableAngleMax = false
  EnableAngleMin = false
  EnableLengthMax = false
  EnableLengthMin = false
  JointType = 5 (Distance)
  LengthMax = 0
  LengthMin = 0
  Placement1 = pos=(0,-2.84e-14,9.8) rot=(0,-1,0;1.5708rad)
  Placement2 = pos=(396.3,-10,6.846e-13) rot=(0.57735,0.57735,0.57735;4.18879rad)
  Reference1 = -> free_wheel_support [Face16,Face16]
  Reference2 = -> _2020_340mm002 [Face49,Vertex25]
  Suppressed = false
FEATURE [App::FeaturePython] Joint122  label="Distance111"  # Assembly joint (typed FeaturePython)
  Angle = 0
  AngleMax = 0
  AngleMin = 0
  Detach1 = false
  Detach2 = false
  Distance = 0.5
  Distance2 = 0
  EnableAngleMax = false
  EnableAngleMin = false
  EnableLengthMax = false
  EnableLengthMin = false
  JointType = 5 (Distance)
  LengthMax = 0
  LengthMin = 0
  Placement1 = pos=(-13.2545,36,4.43806) rot=(-0.57735,-0.57735,-0.57735;2.0944rad)
  Placement2 = pos=(264.356,10,2.03855e-11) rot=(-0.57735,-0.57735,-0.57735;2.0944rad)
  Reference1 = -> free_wheel_support [Face1,Vertex4]
  Reference2 = -> CoinAvant__Mirror__1_ [Face1,Vertex16]
  Suppressed = false
FEATURE [App::FeaturePython] Joint123  label="Parallel028"  # Assembly joint (typed FeaturePython)
  Angle = 0
  AngleMax = 0
  AngleMin = 0
  Detach1 = false
  Detach2 = false
  Distance = 0
  Distance2 = 0
  EnableAngleMax = false
  EnableAngleMin = false
  EnableLengthMax = false
  EnableLengthMin = false
  JointType = 6 (Parallel)
  LengthMax = 0
  LengthMin = 0
  Placement1 = pos=(13.3,26,-3.6e-15) rot=(0,0,1;0rad)
  Placement2 = pos=(393,-8.5,-170) rot=(0,1,0;1.5708rad)
  Reference1 = -> free_wheel_support001 [Face7,Vertex24]
  Reference2 = -> _2020_340mm002 [Face46,Vertex98]
  Suppressed = false
FEATURE [App::FeaturePython] Joint124  label="Distance112"  # Assembly joint (typed FeaturePython)
  Angle = 0
  AngleMax = 0
  AngleMin = 0
  Detach1 = false
  Detach2 = false
  Distance = 0
  Distance2 = 0
  EnableAngleMax = false
  EnableAngleMin = false
  EnableLengthMax = false
  EnableLengthMin = false
  JointType = 5 (Distance)
  LengthMax = 0
  LengthMin = 0
  Placement1 = pos=(9.82583,0,7.1e-15) rot=(0,0,1;0rad)
  Placement2 = pos=(393,-6.7,9.11e-14) rot=(0,1,0;1.5708rad)
  Reference1 = -> free_wheel_support001 [Face7,Face7]
  Reference2 = -> _2020_340mm002 [Face46,Vertex98]
  Suppressed = false
FEATURE [App::FeaturePython] Joint125  label="Distance113"  # Assembly joint (typed FeaturePython)
  Angle = 0
  AngleMax = 0
  AngleMin = 0
  Detach1 = false
  Detach2 = false
  Distance = 0
  Distance2 = 0
  EnableAngleMax = false
  EnableAngleMin = false
  EnableLengthMax = false
  EnableLengthMin = false
  JointType = 5 (Distance)
  LengthMax = 0
  LengthMin = 0
  Placement1 = pos=(5.68e-14,-2.84e-14,9.8) rot=(0,-1,0;1.5708rad)
  Placement2 = pos=(396.3,-10,6.846e-13) rot=(0.57735,0.57735,0.57735;4.18879rad)
  Reference1 = -> free_wheel_support001 [Face16,Face16]
  Reference2 = -> _2020_340mm002 [Face49,Vertex100]
  Suppressed = false
FEATURE [App::FeaturePython] Joint126  label="Distance114"  # Assembly joint (typed FeaturePython)
  Angle = 0
  AngleMax = 0
  AngleMin = 0
  Detach1 = false
  Detach2 = false
  Distance = 0.5
  Distance2 = 0
  EnableAngleMax = false
  EnableAngleMin = false
  EnableLengthMax = false
  EnableLengthMin = false
  JointType = 5 (Distance)
  LengthMax = 0
  LengthMin = 0
  Placement1 = pos=(-13.2545,36,4.43806) rot=(-0.57735,-0.57735,-0.57735;2.0944rad)
  Placement2 = pos=(258.514,-27,0.000576762) rot=(0.57735,-0.57735,0.57735;2.0944rad)
  Reference1 = -> free_wheel_support001 [Face1,Face1]
  Reference2 = -> CoinInterieurAvant001 [Face8,Vertex35]
  Suppressed = false
FEATURE [Assembly::JointGroup] Joints
  Group = -> [Joint,GroundedJoint,Joint001,Joint002,Joint004,Joint005,Joint006,Joint007,Joint008,Joint009,Joint010,Joint011,Joint012,Joint013,Joint014,Joint015,Joint016,Joint017,Joint018,Joint019,Joint020,Joint040,Joint041,Joint042,Joint043,Joint044,Joint045,Joint046,Joint047,Joint048,Joint049,Joint050,Joint051,Joint052,Joint053,Joint054,Joint055,Joint056,Joint057,Joint058,Joint059,Joint060,Joint061,Joint062,+64 more]
FEATURE [Assembly::AssemblyObject] Assembly  label="structure-asm"
  Group = -> [Joints,_2020_50mm,_2020_50mm001,_2020_300mm,_2020_300mm001,_2020_300mm002,_2020_300mm003,_2020_300mm004,_2020_300mm005,_2020_300mm006,_2020_300mm007,_2020_340mm,_2020_340mm001,_2020_340mm002,Joint,GroundedJoint,CoinLateralBD,Joint001,Joint002,Joint004,Joint005,Joint006,Joint007,Joint008,Joint009,CoinLateralHD,Joint010,Joint011,Joint012,Joint013,Joint014,Joint015,Joint016,Joint017,Joint018,+109 more]
  Origin = -> Origin
  Type = Assembly

RESOLVED EXTERNAL PARTS (link-assembly join: the EXTERNAL_REF files above that resolve inside this repo's crawl, each included once):
---- part RC-Robot-parts-export.FCStd = doc fcstd_e92a0ad3deb9 ----
FCSTD DOCUMENT  (FreeCAD 1.2R20260120 (Git shallow))
Label: RC-Robot-parts-export
License: All rights reserved
LicenseURL: https://en.wikipedia.org/wiki/All_rights_reserved
objects: Part::Feature×18, Part::Mirroring×7, App::Part×1, App::Point×1
note: 25 computed .brp shape members not serialized (recipe doc carries the construction recipe); baked Part::Feature solids carry a one-line shape summary decoded from their .brp

FEATURE [Part::Feature] Part__Feature  label="Moteur"
  Placement = pos=(0,100,4e-16) rot=(1,0,0;3.14159rad)
  shape: bbox 107.1 x 35.7 x 35.7 mm, 15 faces (baked)
FEATURE [Part::Feature] Part__Feature001  label="MotorMount2020"
  Placement = pos=(0,100,0) rot=(0,0,1;0rad)
  shape: bbox 33 x 41.69 x 93.42 mm, 38 faces (baked)
FEATURE [Part::Feature] Part__Feature002  label="CoinLateral"
  shape: bbox 49.87 x 50 x 46.78 mm, 44 faces (baked)
FEATURE [Part::Feature] Part__Feature003  label="CoinAvant"
  shape: bbox 67.87 x 35 x 45.07 mm, 39 faces (baked)
FEATURE [Part::Feature] Part__Feature004  label="SupportAxeRoulement"
  shape: bbox 43.29 x 27 x 91.82 mm, 54 faces (baked)
FEATURE [Part::Feature] Part__Feature005  label="CoinInterieurAvant"
  Placement = pos=(0,109,0) rot=(0,0,1;0rad)
  shape: bbox 47.61 x 27 x 45.08 mm, 55 faces (baked)
FEATURE [Part::Feature] Part__Feature006  label="CoinInterieurArriere"
  shape: bbox 52.12 x 27 x 29.69 mm, 26 faces (baked)
FEATURE [Part::Feature] Part__Feature007  label="EquerrePlateauElec"
  shape: bbox 26.68 x 10 x 21.23 mm, 24 faces (baked)
FEATURE [Part::Feature] Part__Feature008  label="PlateauElec001"
  shape: bbox 169.5 x 90 x 18.92 mm, 62 faces (baked)
FEATURE [Part::Feature] Part__Feature009  label="GardeBoue"
  shape: bbox 26.6 x 90 x 59.82 mm, 54 faces (baked)
FEATURE [Part::Feature] Part__Feature010  label="2020-50mm"
  Placement = pos=(0,-9,0) rot=(0,0,1;0rad)
  shape: bbox 20 x 20 x 50 mm, 51 faces (baked)
FEATURE [Part::Feature] Part__Feature011  label="2020-300mm"
  shape: bbox 20 x 20 x 300 mm, 51 faces (baked)
FEATURE [Part::Feature] Part__Feature012  label="2020-340mm"
  shape: bbox 20 x 20 x 340 mm, 51 faces (baked)
FEATURE [Part::Mirroring] Part__Mirroring  label="CoinAvant (Mirror #1)"
  Base = (273.69,10,18.0708)
  MirrorPlane = -> Part__Feature003 [Face1]
  Normal = (0,1,2e-16)
  Placement = pos=(0,34,0) rot=(0,0,1;0rad)
  Source = -> Part__Feature003
FEATURE [Part::Mirroring] Part__Mirroring001  label="CoinInterieurAvant (Mirror #2)"
  Base = (268.379,82,19.5183)
  MirrorPlane = -> Part__Feature005 [Face8]
  Normal = (0,-1,2e-16)
  Placement = pos=(0,89,0) rot=(0,0,1;0rad)
  Source = -> Part__Feature005
FEATURE [Part::Mirroring] Part__Mirroring002  label="CoinInterieurArriere (Mirror #3)"
  Base = (-70.5769,-27,-24.7156)
  MirrorPlane = -> Part__Feature006 [Face12]
  Normal = (-5e-16,-1,3e-16)
  Source = -> Part__Feature006
FEATURE [Part::Mirroring] Part__Mirroring003  label="CoinLateral (Mirror #4)"
  Base = (-45.1472,-5e-15,49.4406)
  MirrorPlane = -> Part__Feature002 [Face9]
  Normal = (0.0937419,5.2e-15,0.995597)
  Placement = pos=(0,0,-159) rot=(0,0,1;0rad)
  Source = -> Part__Feature002
FEATURE [Part::Mirroring] Part__Mirroring004  label="CoinLateralHG"
  Base = (-71.9119,-20,31.8722)
  MirrorPlane = -> Part__Feature002 [Face11]
  Normal = (0,1,2e-16)
  Source = -> Part__Feature002
FEATURE [Part::Mirroring] Part__Mirroring005  label="CoinLateralBG"
  Base = (-68.1623,-20,-87.3039)
  MirrorPlane = -> Part__Mirroring003 [Face11]
  Normal = (-1e-15,1,-1.06e-14)
  Source = -> Part__Mirroring003
FEATURE [Part::Feature] Part__Feature013  label="CoinLateralHD"
  shape: bbox 49.87 x 50 x 46.78 mm, 44 faces (baked)
FEATURE [Part::Feature] Part__Feature014  label="CoinLateral001"
  shape: bbox 49.87 x 50 x 46.78 mm, 44 faces (baked)
FEATURE [Part::Mirroring] Part__Mirroring006  label="CoinLateralBD"
  Base = (-45.1472,-5e-15,49.4406)
  MirrorPlane = -> Part__Feature014 [Face9]
  Normal = (0.0937419,5.2e-15,0.995597)
  Placement = pos=(0,0,-159) rot=(0,0,1;0rad)
  Source = -> Part__Feature014
FEATURE [Part::Feature] Part__Feature015  label="CoinAvant001"
  shape: bbox 67.87 x 35 x 45.07 mm, 39 faces (baked)
FEATURE [Part::Feature] Part__Feature016  label="CoinInterieurArriere001"
  shape: bbox 52.12 x 27 x 29.69 mm, 26 faces (baked)
FEATURE [Part::Feature] Part__Feature017  label="CoinInterieurAvant001"
  Placement = pos=(0,109,0) rot=(0,0,1;0rad)
  shape: bbox 47.61 x 27 x 45.08 mm, 55 faces (baked)
FEATURE [App::Part] Part  label="motor-mounted"
  Group = -> [Part__Feature001,Part__Feature]
  Origin = -> Origin
FEATURE [App::Point] Origin001  label="Origine"
  Role = Origin
---- part actuators-parts/wheel.FCStd = doc fcstd_ab4e4ed80432 ----
FCSTD DOCUMENT  (FreeCAD 1.2R20260204 (Git shallow))
Label: wheel
License: All rights reserved
LicenseURL: https://en.wikipedia.org/wiki/All_rights_reserved
objects: Sketcher::SketchObject×12, PartDesign::Pad×7, App::Point×5, PartDesign::Chamfer×5, PartDesign::Body×4, PartDesign::Pocket×4, PartDesign::Fillet×2, PartDesign::Mirrored×2, App::Link×1, PartDesign::Groove×1, App::Part×1
note: 89 computed .brp shape members not serialized (recipe doc carries the construction recipe); baked Part::Feature solids carry a one-line shape summary decoded from their .brp

FEATURE [App::Link] Link  label="Link(Flasque)"
  LinkPlacement = pos=(-30,6.79493e-06,0) rot=(0,0,1;0rad)
  LinkedObject = -> Body008
  Placement = pos=(-30,6.79493e-06,0) rot=(0,0,1;0rad)
FEATURE [App::Point] Origin045  label="Origine"
  Role = Origin
FEATURE [App::Point] Origin046  label="Origine001"
  Role = Origin
FEATURE [App::Point] Origin047  label="Origine002"
  Role = Origin
FEATURE [App::Point] Origin048  label="Origine003"
  Role = Origin
FEATURE [App::Point] Origin049  label="Origine004"
  Role = Origin
FEATURE [Sketcher::SketchObject] Sketch011
  ArcFitTolerance = 1e-06
  AttachmentSupport = -> [YZ_Plane005]
  ExternalTypes = [0]
  FullyConstrained = true
  MakeInternals = false
  MapMode = 5
  Placement = pos=(0,0,0) rot=(0.57735,0.57735,0.57735;2.0944rad)
  sketch-geometry (2):
    g0: Circle CenterX=0 CenterY=0 CenterZ=0 NormalX=0 NormalY=0 NormalZ=1 AngleXU=0 Radius=54
    g1: Circle CenterX=0 CenterY=0 CenterZ=0 NormalX=0 NormalY=0 NormalZ=1 AngleXU=0 Radius=40
  constraints (4):
    c: Coincident(g0,g-1)
    c: Diameter(g0) = 108
    c: Coincident(g1,g0)
    c: Diameter(g1) = 80
FEATURE [PartDesign::Pad] Pad007
  AlongSketchNormal = false
  Direction = (1,0,0)
  Length = 50
  Length2 = 10
  Placement = pos=(0,0,0) rot=(1,1,1;2.0944rad)
  Profile = -> Sketch011
  ReferenceAxis = -> Sketch011 [N_Axis]
  Refine = true
  SideType = 2
  Suppressed = false
  Type = 0
  Type2 = 0
FEATURE [PartDesign::Fillet] Fillet
  Base = -> Pad007 [Edge3,Edge2]
  BaseFeature = -> Pad007
  Placement = pos=(0,0,0) rot=(1,1,1;2.0944rad)
  Radius = 3
  Refine = true
  SupportTransform = false
  Suppressed = false
  UseAllEdges = false
FEATURE [PartDesign::Chamfer] Chamfer
  Angle = 45
  Base = -> Fillet [Edge10,Face6]
  BaseFeature = -> Fillet
  ChamferType = 0
  FlipDirection = false
  Placement = pos=(0,0,0) rot=(1,1,1;2.0944rad)
  Refine = true
  Size = 1
  Size2 = 1
  SupportTransform = false
  Suppressed = false
  UseAllEdges = false
FEATURE [PartDesign::Body] Body005  label="InsertTPU-Pneu"
  AllowCompound = true
  Group = -> [Sketch011,Pad007,Fillet,Chamfer]
  Origin = -> Origin006
  Tip = -> Chamfer
FEATURE [Sketcher::SketchObject] Sketch012
  ArcFitTolerance = 1e-06
  AttachmentSupport = -> [YZ_Plane006]
  ExternalTypes = [0]
  FullyConstrained = true
  MakeInternals = false
  MapMode = 5
  Placement = pos=(0,0,0) rot=(0.57735,0.57735,0.57735;2.0944rad)
  sketch-geometry (1):
    g0: Circle CenterX=0 CenterY=0 CenterZ=0 NormalX=0 NormalY=0 NormalZ=1 AngleXU=0 Radius=40.5
  constraints (2):
    c: Coincident(g0,g-1)
    c: Diameter(g0) = 81
FEATURE [PartDesign::Pad] Pad008
  AlongSketchNormal = false
  Direction = (1,0,0)
  Length = 50
  Length2 = 10
  Placement = pos=(0,0,0) rot=(1,1,1;2.0944rad)
  Profile = -> Sketch012
  ReferenceAxis = -> Sketch012 [N_Axis]
  Refine = true
  SideType = 2
  Suppressed = false
  Type = 0
  Type2 = 0
FEATURE [Sketcher::SketchObject] Sketch013
  ArcFitTolerance = 1e-06
  AttachmentSupport = -> [YZ_Plane007]
  ExternalTypes = [0]
  FullyConstrained = true
  MakeInternals = false
  MapMode = 5
  Placement = pos=(0,0,0) rot=(0.57735,0.57735,0.57735;2.0944rad)
  sketch-geometry (2):
    g0: Circle CenterX=0 CenterY=0 CenterZ=0 NormalX=0 NormalY=0 NormalZ=1 AngleXU=0 Radius=50
    g1: Circle CenterX=0 CenterY=0 CenterZ=0 NormalX=0 NormalY=0 NormalZ=1 AngleXU=0 Radius=58.75
  constraints (4):
    c: Coincident(g0,g-1)
    c: Diameter(g0) = 100
    c: Coincident(g1,g0)
    c: Diameter(g1) = 117.5
FEATURE [PartDesign::Pad] Pad009
  AlongSketchNormal = false
  Direction = (1,0,0)
  Length = 50
  Length2 = 10
  Placement = pos=(0,0,0) rot=(1,1,1;2.0944rad)
  Profile = -> Sketch013
  ReferenceAxis = -> Sketch013 [N_Axis]
  Refine = true
  SideType = 2
  Suppressed = false
  Type = 0
  Type2 = 0
FEATURE [Sketcher::SketchObject] Sketch014
  ArcFitTolerance = 1e-06
  AttachmentSupport = -> [Pad009]
  ExternalTypes = [0]
  FullyConstrained = true
  MakeInternals = false
  MapMode = 5
  Placement = pos=(25,0,0) rot=(0.57735,0.57735,0.57735;2.0944rad)
  sketch-geometry (1):
    g0: Circle CenterX=0 CenterY=0 CenterZ=0 NormalX=0 NormalY=0 NormalZ=1 AngleXU=0 Radius=36
  constraints (2):
    c: Coincident(g0,g-3)
    c: Diameter(g0) = 72
FEATURE [PartDesign::Pad] Pad010
  AlongSketchNormal = false
  BaseFeature = -> Pad009
  Direction = (1,0,0)
  Length = 2.5
  Length2 = 10
  Placement = pos=(0,0,0) rot=(1,1,1;2.0944rad)
  Profile = -> Sketch014
  ReferenceAxis = -> Sketch014 [N_Axis]
  Refine = true
  SideType = 0
  Suppressed = false
  Type = 0
  Type2 = 0
FEATURE [PartDesign::Mirrored] Mirrored
  BaseFeature = -> Pad010
  MirrorPlane = -> YZ_Plane007
  Originals = -> [Pad010]
  Placement = pos=(0,0,0) rot=(1,1,1;2.0944rad)
  Refine = true
  Suppressed = false
  TransformMode = 0
FEATURE [PartDesign::Fillet] Fillet001
  Base = -> Mirrored [Edge11,Edge10]
  BaseFeature = -> Mirrored
  Placement = pos=(0,0,0) rot=(1,1,1;2.0944rad)
  Radius = 3
  Refine = true
  SupportTransform = false
  Suppressed = false
  UseAllEdges = false
FEATURE [PartDesign::Body] Body007  label="Pneu"
  AllowCompound = true
  Group = -> [Sketch013,Pad009,Sketch014,Pad010,Mirrored,Fillet001]
  Origin = -> Origin009
  Tip = -> Fillet001
FEATURE [Sketcher::SketchObject] Sketch015
  ArcFitTolerance = 1e-06
  AttachmentSupport = -> [Pad008]
  ExternalTypes = [0]
  FullyConstrained = true
  MakeInternals = false
  MapMode = 5
  Placement = pos=(25,0,0) rot=(0.57735,0.57735,0.57735;2.0944rad)
  sketch-geometry (1):
    g0: Circle CenterX=0 CenterY=0 CenterZ=0 NormalX=0 NormalY=0 NormalZ=1 AngleXU=0 Radius=35
  constraints (2):
    c: Coincident(g0,g-1)
    c: Diameter(g0) = 70
FEATURE [PartDesign::Pad] Pad011
  AlongSketchNormal = false
  BaseFeature = -> Pad008
  Direction = (1,0,0)
  Length = 2
  Length2 = 10
  Placement = pos=(0,0,0) rot=(1,1,1;2.0944rad)
  Profile = -> Sketch015
  ReferenceAxis = -> Sketch015 [N_Axis]
  Refine = true
  SideType = 0
  Suppressed = false
  Type = 0
  Type2 = 0
FEATURE [PartDesign::Mirrored] Mirrored001
  BaseFeature = -> Pad011
  MirrorPlane = -> YZ_Plane006
  Originals = -> [Pad011]
  Placement = pos=(0,0,0) rot=(1,1,1;2.0944rad)
  Refine = true
  Suppressed = false
  TransformMode = 0
FEATURE [Sketcher::SketchObject] Sketch016
  ArcFitTolerance = 1e-06
  AttachmentSupport = -> [Mirrored001]
  ExternalTypes = [0]
  FullyConstrained = true
  MakeInternals = false
  MapMode = 5
  Placement = pos=(27,0,0) rot=(0.57735,0.57735,0.57735;2.0944rad)
  sketch-geometry (5):
    g0: Circle CenterX=0 CenterY=30 CenterZ=0 NormalX=0 NormalY=0 NormalZ=1 AngleXU=0 Radius=2.2
    g1: Circle CenterX=-30 CenterY=0 CenterZ=0 NormalX=0 NormalY=0 NormalZ=1 AngleXU=0 Radius=2.2
    g2: Circle CenterX=0 CenterY=-30 CenterZ=0 NormalX=0 NormalY=0 NormalZ=1 AngleXU=0 Radius=2.2
    g3: Circle CenterX=30 CenterY=0 CenterZ=0 NormalX=0 NormalY=0 NormalZ=1 AngleXU=0 Radius=2.2
    g4: Circle [constr] CenterX=0 CenterY=0 CenterZ=0 NormalX=0 NormalY=0 NormalZ=1 AngleXU=0 Radius=30
  constraints (14):
    c: PointOnObject(g0,g-2)
    c: PointOnObject(g1,g-1)
    c: PointOnObject(g2,g-2)
    c: PointOnObject(g3,g-1)
    c: Coincident(g4,g-1)
    c: PointOnObject(g0,g4)
    c: PointOnObject(g1,g4)
    c: PointOnObject(g3,g4)
    c: PointOnObject(g2,g4)
    c: Equal(g3,g0)
    c: Equal(g3,g1)
    c: Equal(g3,g2)
    c: Diameter(g3) = 4.4
    c: Diameter(g4) = 60
FEATURE [PartDesign::Pocket] Pocket003
  AlongSketchNormal = false
  BaseFeature = -> Mirrored001
  Direction = (-1,0,0)
  Length = 15
  Length2 = 10
  Placement = pos=(0,0,0) rot=(1,1,1;2.0944rad)
  Profile = -> Sketch016
  ReferenceAxis = -> Sketch016 [N_Axis]
  Refine = true
  SideType = 0
  Suppressed = false
  Type = 1
  Type2 = 0
FEATURE [Sketcher::SketchObject] Sketch017
  ArcFitTolerance = 1e-06
  AttachmentSupport = -> [YZ_Plane008]
  ExternalTypes = [0]
  FullyConstrained = true
  MakeInternals = false
  MapMode = 5
  Placement = pos=(0,0,0) rot=(0.57735,0.57735,0.57735;2.0944rad)
  sketch-geometry (6):
    g0: Circle CenterX=0 CenterY=0 CenterZ=0 NormalX=0 NormalY=0 NormalZ=1 AngleXU=0 Radius=25
    g1: Circle CenterX=0 CenterY=0 CenterZ=0 NormalX=0 NormalY=0 NormalZ=1 AngleXU=0 Radius=50
    g2: Circle CenterX=0 CenterY=30 CenterZ=0 NormalX=0 NormalY=0 NormalZ=1 AngleXU=0 Radius=1.6
    g3: Circle CenterX=30 CenterY=0 CenterZ=0 NormalX=0 NormalY=0 NormalZ=1 AngleXU=0 Radius=1.6
    g4: Circle CenterX=-30 CenterY=0 CenterZ=0 NormalX=0 NormalY=0 NormalZ=1 AngleXU=0 Radius=1.6
    g5: Circle CenterX=0 CenterY=-30 CenterZ=0 NormalX=0 NormalY=0 NormalZ=1 AngleXU=0 Radius=1.6
  constraints (12):
    c: Coincident(g0,g-1)
    c: Coincident(g1,g0)
    c: Coincident(g2,g-3)
    c: Coincident(g3,g-6)
    c: Coincident(g4,g-4)
    c: Coincident(g5,g-5)
    c: Equal(g5,g4)
    c: Equal(g5,g2)
    c: Equal(g5,g3)
    c: Diameter(g5) = 3.2
    c: Diameter(g0) = 50
    c: Diameter(g1) = 100
FEATURE [PartDesign::Pad] Pad012
  AlongSketchNormal = false
  Direction = (1,0,0)
  Length = 3
  Length2 = 10
  Placement = pos=(0,0,0) rot=(1,1,1;2.0944rad)
  Profile = -> Sketch017
  ReferenceAxis = -> Sketch017 [N_Axis]
  Refine = true
  SideType = 0
  Suppressed = false
  Type = 0
  Type2 = 0
FEATURE [PartDesign::Body] Body008  label="Flasque"
  AllowCompound = true
  Group = -> [Sketch017,Pad012]
  Origin = -> Origin011
  Placement = pos=(27,0,0) rot=(0,0,1;0rad)
  Tip = -> Pad012
FEATURE [Sketcher::SketchObject] Sketch018
  ArcFitTolerance = 1e-06
  AttachmentSupport = -> [Pocket003]
  ExternalTypes = [0]
  FullyConstrained = true
  MakeInternals = false
  MapMode = 5
  Placement = pos=(27,0,0) rot=(0.57735,0.57735,0.57735;2.0944rad)
  sketch-geometry (3):
    g0: ArcOfCircle CenterX=0 CenterY=0 CenterZ=0 NormalX=0 NormalY=0 NormalZ=1 AngleXU=0 Radius=19.7231 StartAngle=2.88792 EndAngle=8.10766
    g1: LineSegment StartX=-19.0919 StartY=4.94975 StartZ=0 EndX=-4.94975 EndY=19.0919 EndZ=0
    g2: LineSegment [constr] StartX=0 StartY=0 StartZ=0 EndX=-12.0208 EndY=12.0208 EndZ=0
  constraints (8):
    c: Coincident(g0,g-1)
    c: Coincident(g1,g0)
    c: Coincident(g1,g0)
    c: Distance(g1) = 20
    c: Coincident(g2,g0)
    c: Symmetric(g0,g0,g2)
    c: Angle(g-2,g2) = 0.785398
    c: Distance(g2) = 17
FEATURE [PartDesign::Pad] Pad013
  AlongSketchNormal = false
  BaseFeature = -> Pocket003
  Direction = (1,0,0)
  Length = 13
  Length2 = 10
  Placement = pos=(0,0,0) rot=(1,1,1;2.0944rad)
  Profile = -> Sketch018
  ReferenceAxis = -> Sketch018 [N_Axis]
  Refine = true
  SideType = 0
  Suppressed = false
  Type = 0
  Type2 = 0
FEATURE [Sketcher::SketchObject] Sketch019
  ArcFitTolerance = 1e-06
  AttachmentOffset = pos=(0,0,0) rot=(0,0,1;1.5708rad)
  AttachmentSupport = -> [Pad013]
  ExternalTypes = [0]
  FullyConstrained = true
  MakeInternals = false
  MapMode = 5
  Placement = pos=(-2.7e-15,-12.0208,12.0208) rot=(1,0,0;0.785398rad)
  sketch-geometry (2):
    g0: Circle CenterX=35 CenterY=0 CenterZ=0 NormalX=0 NormalY=0 NormalZ=1 AngleXU=0 Radius=2.1
    g1: Circle [constr] CenterX=35 CenterY=0 CenterZ=0 NormalX=0 NormalY=0 NormalZ=1 AngleXU=0 Radius=5
  constraints (5):
    c: PointOnObject(g0,g-1)
    c: Diameter(g0) = 4.2
    c: Coincident(g1,g0)
    c: Tangent(g1,g-3)
    c: Diameter(g1) = 10
FEATURE [Sketcher::SketchObject] Sketch020
  ArcFitTolerance = 1e-06
  AttachmentSupport = -> [Pad013]
  ExternalTypes = [0]
  FullyConstrained = true
  MakeInternals = false
  MapMode = 5
  Placement = pos=(40,0,0) rot=(0.57735,0.57735,0.57735;2.0944rad)
  sketch-geometry (1):
    g0: Circle CenterX=0 CenterY=0 CenterZ=0 NormalX=0 NormalY=0 NormalZ=1 AngleXU=0 Radius=3.2
  constraints (2):
    c: Coincident(g0,g-1)
    c: Diameter(g0) = 6.4
FEATURE [PartDesign::Pocket] Pocket004
  AlongSketchNormal = false
  BaseFeature = -> Pad013
  Direction = (-1,0,0)
  Length = 15
  Length2 = 10
  Placement = pos=(0,0,0) rot=(1,1,1;2.0944rad)
  Profile = -> Sketch020
  ReferenceAxis = -> Sketch020 [N_Axis]
  Refine = true
  SideType = 0
  Suppressed = false
  Type = 1
  Type2 = 0
FEATURE [PartDesign::Pocket] Pocket005
  AlongSketchNormal = false
  BaseFeature = -> Pocket004
  Direction = (0,0.707107,-0.707107)
  Length = 17
  Length2 = 10
  Placement = pos=(0,0,0) rot=(1,1,1;2.0944rad)
  Profile = -> Sketch019
  ReferenceAxis = -> Sketch019 [N_Axis]
  Refine = true
  SideType = 0
  Suppressed = false
  Type = 0
  Type2 = 0
FEATURE [Sketcher::SketchObject] Sketch021
  ArcFitTolerance = 1e-06
  AttachmentSupport = -> [Pocket005]
  ExternalGeometry = -> [Pocket005]
  ExternalTypes = [0]
  FullyConstrained = true
  MakeInternals = false
  MapMode = 5
  Placement = pos=(40,0,0) rot=(0.57735,0.57735,0.57735;2.0944rad)
  sketch-geometry (7):
    g0: LineSegment [constr] StartX=0 StartY=0 StartZ=0 EndX=-12.0208 EndY=12.0208 EndZ=0
    g1: LineSegment StartX=-11.0662 StartY=5.90434 StartZ=0 EndX=-8.66206 EndY=3.50018 EndZ=0
    g2: LineSegment StartX=-8.66206 StartY=3.50018 StartZ=0 EndX=-3.50018 EndY=8.66206 EndZ=0
    g3: LineSegment StartX=-3.50018 StartY=8.66206 StartZ=0 EndX=-5.90434 EndY=11.0662 EndZ=0
    g4: LineSegment StartX=-5.90434 StartY=11.0662 StartZ=0 EndX=-11.0662 EndY=5.90434 EndZ=0
    g5: GeomPoint [constr] X=-7.2832 Y=7.2832 Z=0
    g6: GeomPoint [constr] X=-8.48528 Y=8.48528 Z=0
  constraints (17):
    c: Coincident(g0,g-1)
    c: Symmetric(g-3,g-3,g0)
    c: Coincident(g1,g2)
    c: Coincident(g2,g3)
    c: Coincident(g3,g4)
    c: Coincident(g4,g1)
    c: Parallel(g2,g4)
    c: Parallel(g1,g3)
    c: Symmetric(g2,g1,g5)
    c: PointOnObject(g5,g0)
    c: Perpendicular(g1,g2)
    c: Perpendicular(g0,g4)
    c: Distance(g3) = 3.4
    c: Distance(g2) = 7.3
    c: PointOnObject(g6,g4)
    c: PointOnObject(g6,g0)
    c: Distance(g6,g0) = 5
FEATURE [PartDesign::Pocket] Pocket006
  AlongSketchNormal = false
  BaseFeature = -> Pocket005
  Direction = (-1,0,0)
  Length = 9
  Length2 = 10
  Placement = pos=(0,0,0) rot=(1,1,1;2.0944rad)
  Profile = -> Sketch021
  ReferenceAxis = -> Sketch021 [N_Axis]
  Refine = true
  SideType = 0
  Suppressed = false
  Type = 0
  Type2 = 0
FEATURE [Sketcher::SketchObject] Sketch067
  ArcFitTolerance = 1e-06
  AttachmentSupport = -> [XZ_Plane006]
  ExternalTypes = [0]
  FullyConstrained = true
  MakeInternals = false
  MapMode = 5
  Placement = pos=(0,0,0) rot=(1,0,0;1.5708rad)
  sketch-geometry (8):
    g0: LineSegment StartX=-27.5 StartY=0 StartZ=0 EndX=-27.5 EndY=13.7 EndZ=0
    g1: LineSegment StartX=-27.5 StartY=13.7 StartZ=0 EndX=-26 EndY=13.7 EndZ=0
    g2: LineSegment StartX=-26 StartY=13.7 StartZ=0 EndX=-26 EndY=12.2 EndZ=0
    g3: LineSegment StartX=-26 StartY=12.2 StartZ=0 EndX=-19.3 EndY=12.2 EndZ=0
    g4: LineSegment StartX=-19.3 StartY=12.2 StartZ=0 EndX=-19.3 EndY=8.5 EndZ=0
    g5: LineSegment StartX=-19.3 StartY=8.5 StartZ=0 EndX=0 EndY=8.5 EndZ=0
    g6: LineSegment StartX=0 StartY=8.5 StartZ=0 EndX=0 EndY=0 EndZ=0
    g7: LineSegment StartX=0 StartY=0 StartZ=0 EndX=-27.5 EndY=0 EndZ=0
  constraints (23):
    c: PointOnObject(g0,g-1)
    c: Vertical(g0)
    c: Coincident(g0,g1)
    c: Coincident(g1,g2)
    c: Vertical(g2)
    c: Coincident(g2,g3)
    c: Horizontal(g3)
    c: Coincident(g3,g4)
    c: Vertical(g4)
    c: Coincident(g4,g5)
    c: PointOnObject(g5,g-2)
    c: Horizontal(g5)
    c: Coincident(g5,g6)
    c: Coincident(g6,g-1)
    c: Coincident(g6,g7)
    c: Coincident(g7,g0)
    c: PointOnObject(g0,g-3)
    c: Horizontal(g1)
    c: DistanceX(g1,g1) = 1.5
    c: DistanceX(g0,g3) = 8.2
    c: DistanceY(g0,g0) = 13.7
    c: DistanceY(g2) = 12.2
    c: DistanceY(g4) = 8.5
FEATURE [PartDesign::Groove] Groove
  Angle = 360
  Angle2 = 0
  Axis = (1,0,0)
  Base = (0,0,0)
  BaseFeature = -> Pocket006
  Placement = pos=(0,0,0) rot=(1,1,1;2.0944rad)
  Profile = -> Sketch067
  ReferenceAxis = -> Sketch067 [H_Axis]
  Refine = true
  Reversed = true
  Suppressed = false
  Type = 0
FEATURE [PartDesign::Chamfer] Chamfer025
  Angle = 45
  Base = -> Groove [Edge54]
  BaseFeature = -> Groove
  ChamferType = 0
  FlipDirection = false
  Placement = pos=(0,0,0) rot=(1,1,1;2.0944rad)
  Refine = true
  Size = 1
  Size2 = 1
  SupportTransform = false
  Suppressed = false
  UseAllEdges = false
FEATURE [PartDesign::Chamfer] Chamfer026
  Angle = 45
  Base = -> Chamfer025 [Edge5]
  BaseFeature = -> Chamfer025
  ChamferType = 0
  FlipDirection = false
  Placement = pos=(0,0,0) rot=(1,1,1;2.0944rad)
  Refine = true
  Size = 0.4
  Size2 = 1
  SupportTransform = false
  Suppressed = false
  UseAllEdges = false
FEATURE [PartDesign::Chamfer] Chamfer034
  Angle = 45
  Base = -> Chamfer026 [Edge15,Edge17,Edge18,Edge16,Edge28,Edge24,Edge22,Edge26,Edge14]
  BaseFeature = -> Chamfer026
  ChamferType = 0
  FlipDirection = false
  Placement = pos=(0,0,0) rot=(1,1,1;2.0944rad)
  Refine = true
  Size = 1
  Size2 = 1
  SupportTransform = false
  Suppressed = false
  UseAllEdges = false
FEATURE [PartDesign::Chamfer] Chamfer035
  Angle = 45
  Base = -> Chamfer034 [Edge56,Edge54,Edge57,Edge59]
  BaseFeature = -> Chamfer034
  ChamferType = 0
  FlipDirection = false
  Placement = pos=(0,0,0) rot=(1,1,1;2.0944rad)
  Refine = true
  Size = 1
  Size2 = 1
  SupportTransform = false
  Suppressed = false
  UseAllEdges = false
FEATURE [PartDesign::Body] Body006  label="Core-Wheel"
  AllowCompound = true
  Group = -> [Sketch012,Pad008,Sketch015,Pad011,Mirrored001,Sketch016,Pocket003,Sketch018,Pad013,Sketch019,Sketch020,Pocket004,Pocket005,Sketch021,Pocket006,Sketch067,Groove,Chamfer025,Chamfer026,Chamfer034,Chamfer035]
  Origin = -> Origin007
  Tip = -> Chamfer035
FEATURE [App::Part] Part001  label="EnsembleRoue"
  Group = -> [Body005,Body006,Body007,Body008,Link]
  Origin = -> Origin008
  Placement = pos=(-145,0,0) rot=(0,0,1;0rad)
---- part mecanical-parts/free-wheel-support.FCStd = doc fcstd_5c77388d503b ----
FCSTD DOCUMENT  (FreeCAD 1.2R20260204 (Git shallow))
Label: free-wheel-support
License: All rights reserved
LicenseURL: https://en.wikipedia.org/wiki/All_rights_reserved
objects: PartDesign::Chamfer×8, Sketcher::SketchObject×7, PartDesign::Pocket×6, App::Point×1, PartDesign::Pad×1, PartDesign::Body×1
note: 60 computed .brp shape members not serialized (recipe doc carries the construction recipe); baked Part::Feature solids carry a one-line shape summary decoded from their .brp

FEATURE [App::Point] Origin001  label="Origine"
  Role = Origin
FEATURE [Sketcher::SketchObject] Sketch
  ArcFitTolerance = 1e-06
  AttachmentSupport = -> [Origin]
  ExternalTypes = [0]
  FullyConstrained = true
  MakeInternals = false
  MapMode = 5
  Placement = pos=(0,0,0) rot=(1,0,0;1.5708rad)
  sketch-geometry (8):
    g0: LineSegment StartX=0 StartY=0 StartZ=0 EndX=0 EndY=20 EndZ=0
    g1: LineSegment StartX=0 StartY=20 StartZ=0 EndX=-37 EndY=20 EndZ=0
    g2: LineSegment [constr] StartX=-37 StartY=20 StartZ=0 EndX=-37 EndY=0 EndZ=0
    g3: LineSegment [constr] StartX=-37 StartY=0 StartZ=0 EndX=0 EndY=0 EndZ=0
    g4: LineSegment StartX=0 StartY=0 StartZ=0 EndX=20 EndY=0 EndZ=0
    g5: LineSegment StartX=20 StartY=0 StartZ=0 EndX=20 EndY=-8 EndZ=0
    g6: LineSegment StartX=20 StartY=-8 StartZ=0 EndX=-37 EndY=-8 EndZ=0
    g7: LineSegment StartX=-37 StartY=-8 StartZ=0 EndX=-37 EndY=20 EndZ=0
  constraints (22):
    c: Coincident(g0,g1)
    c: Coincident(g1,g2)
    c: Coincident(g2,g3)
    c: Coincident(g3,g0)
    c: Vertical(g0)
    c: Vertical(g2)
    c: Horizontal(g1)
    c: Horizontal(g3)
    c: Coincident(g0,g-1)
    c: DistanceY(g0,g0) = 20
    c: Coincident(g4,g0)
    c: PointOnObject(g4,g-1)
    c: Coincident(g5,g4)
    c: Vertical(g5)
    c: Coincident(g6,g5)
    c: Horizontal(g6)
    c: Coincident(g7,g6)
    c: Coincident(g7,g1)
    c: Vertical(g7)
    c: Distance(g5,g5) = 8
    c: Distance(g4,g4) = 20
    c: DistanceX(g1,g1) = 37
FEATURE [PartDesign::Pad] Pad
  Direction = (0,-1,2e-16)
  Length = 72
  Length2 = 10
  Profile = -> Sketch
  ReferenceAxis = -> Sketch [N_Axis]
  Refine = true
  SideType = 2
  Suppressed = false
  Type = 0
  Type2 = 0
FEATURE [Sketcher::SketchObject] Sketch001
  ArcFitTolerance = 1e-06
  AttachmentSupport = -> [Pad]
  ExternalGeometry = -> [Pad]
  ExternalTypes = [0,0]
  FullyConstrained = true
  MakeInternals = false
  MapMode = 5
  Placement = pos=(0,4.4e-15,20) rot=(0,0,1;0rad)
  sketch-geometry (1):
    g0: Circle CenterX=-18.5 CenterY=5e-16 CenterZ=0 NormalX=0 NormalY=0 NormalZ=1 AngleXU=0 Radius=4.2
  constraints (2):
    c: Symmetric(g-4,g-3,g0)
    c: Diameter(g0) = 8.4
FEATURE [PartDesign::Pocket] Pocket
  BaseFeature = -> Pad
  Direction = (0,0,-1)
  Length = 5
  Length2 = 5
  Profile = -> Sketch001
  ReferenceAxis = -> Sketch001 [N_Axis]
  Refine = true
  SideType = 0
  Suppressed = false
  Type = 1
  Type2 = 0
FEATURE [Sketcher::SketchObject] Sketch002
  ArcFitTolerance = 1e-06
  AttachmentSupport = -> [Pocket]
  ExternalGeometry = -> [Pocket]
  ExternalTypes = [0]
  FullyConstrained = true
  MakeInternals = false
  MapMode = 5
  Placement = pos=(0,-1.8e-15,-8) rot=(1,0,0;3.14159rad)
  sketch-geometry (1):
    g0: Circle CenterX=-18.5 CenterY=0 CenterZ=0 NormalX=0 NormalY=0 NormalZ=1 AngleXU=0 Radius=16.5
  constraints (2):
    c: Coincident(g0,g-3)
    c: Diameter(g0) = 33
FEATURE [PartDesign::Pocket] Pocket001
  BaseFeature = -> Pocket
  Direction = (0,0,1)
  Length = 10
  Length2 = 5
  Profile = -> Sketch002
  ReferenceAxis = -> Sketch002 [N_Axis]
  Refine = true
  SideType = 0
  Suppressed = false
  Type = 0
  Type2 = 0
FEATURE [Sketcher::SketchObject] Sketch003
  ArcFitTolerance = 1e-06
  AttachmentSupport = -> [Pocket001]
  ExternalGeometry = -> [Pocket001]
  ExternalTypes = [0]
  FullyConstrained = true
  MakeInternals = false
  MapMode = 5
  Placement = pos=(0,0,2) rot=(1,0,0;3.14159rad)
  sketch-geometry (7):
    g0: LineSegment StartX=-10.9944 StartY=0 StartZ=0 EndX=-14.7472 EndY=6.5 EndZ=0
    g1: LineSegment StartX=-14.7472 StartY=6.5 StartZ=0 EndX=-22.2528 EndY=6.5 EndZ=0
    g2: LineSegment StartX=-22.2528 StartY=6.5 StartZ=0 EndX=-26.0056 EndY=-1.15e-14 EndZ=0
    g3: LineSegment StartX=-26.0056 StartY=-1.15e-14 StartZ=0 EndX=-22.2528 EndY=-6.5 EndZ=0
    g4: LineSegment StartX=-22.2528 StartY=-6.5 StartZ=0 EndX=-14.7472 EndY=-6.5 EndZ=0
    g5: LineSegment StartX=-14.7472 StartY=-6.5 StartZ=0 EndX=-10.9944 EndY=0 EndZ=0
    g6: Circle [constr] CenterX=-18.5 CenterY=-5e-15 CenterZ=0 NormalX=0 NormalY=0 NormalZ=1 AngleXU=0 Radius=7.50555
  constraints (16):
    c: Coincident(g0,g1)
    c: Coincident(g1,g2)
    c: Coincident(g2,g3)
    c: Coincident(g3,g4)
    c: Coincident(g4,g5)
    c: Coincident(g5,g0)
    c: Equal(g0, g1-g5) x5
    c: PointOnObject(g0,g6)
    c: PointOnObject(g1,g6)
    c: PointOnObject(g2,g6)
    c: PointOnObject(g3,g6)
    c: PointOnObject(g4,g6)
    c: PointOnObject(g5,g6)
    c: Coincident(g6,g-3)
    c: PointOnObject(g5,g-1)
    c: Distance(g4,g1) = 13
FEATURE [PartDesign::Pocket] Pocket002
  BaseFeature = -> Pocket001
  Direction = (0,0,1)
  Length = 6.5
  Length2 = 5
  Profile = -> Sketch003
  ReferenceAxis = -> Sketch003 [N_Axis]
  Refine = true
  SideType = 0
  Suppressed = false
  Type = 0
  Type2 = 0
FEATURE [Sketcher::SketchObject] Sketch004
  ArcFitTolerance = 1e-06
  AttachmentSupport = -> [Pocket002]
  ExternalGeometry = -> [Pocket002]
  ExternalTypes = [0]
  FullyConstrained = true
  MakeInternals = false
  MapMode = 5
  Placement = pos=(0,4.4e-15,20) rot=(0,0,1;0rad)
  sketch-geometry (1):
    g0: Circle CenterX=-18.5 CenterY=0 CenterZ=0 NormalX=0 NormalY=0 NormalZ=1 AngleXU=0 Radius=11.25
  constraints (2):
    c: Coincident(g0,g-3)
    c: Diameter(g0) = 22.5
FEATURE [PartDesign::Pocket] Pocket003
  BaseFeature = -> Pocket002
  Direction = (0,0,-1)
  Length = 1.5
  Length2 = 5
  Profile = -> Sketch004
  ReferenceAxis = -> Sketch004 [N_Axis]
  Refine = true
  SideType = 0
  Suppressed = false
  Type = 0
  Type2 = 0
FEATURE [Sketcher::SketchObject] Sketch005
  ArcFitTolerance = 1e-06
  AttachmentSupport = -> [Pocket003]
  ExternalGeometry = -> [Pocket003]
  ExternalTypes = [0,0]
  FullyConstrained = true
  MakeInternals = false
  MapMode = 5
  Placement = pos=(0,0,-1e-16) rot=(0,0,1;0rad)
  sketch-geometry (3):
    g0: LineSegment [constr] StartX=10 StartY=36 StartZ=0 EndX=10 EndY=-36 EndZ=0
    g1: Circle CenterX=10 CenterY=-26 CenterZ=0 NormalX=0 NormalY=0 NormalZ=1 AngleXU=0 Radius=2.7
    g2: Circle CenterX=10 CenterY=26 CenterZ=0 NormalX=0 NormalY=0 NormalZ=1 AngleXU=0 Radius=2.7
  constraints (7):
    c: Symmetric(g-3,g-3,g0)
    c: Symmetric(g-4,g-4,g0)
    c: PointOnObject(g1,g0)
    c: Symmetric(g2,g1,g-1)
    c: Equal(g2,g1)
    c: Diameter(g2) = 5.4
    c: Distance(g2,g-3) = 10
FEATURE [PartDesign::Pocket] Pocket004
  BaseFeature = -> Pocket003
  Direction = (0,0,-1)
  Length = 10
  Length2 = 5
  Profile = -> Sketch005
  ReferenceAxis = -> Sketch005 [N_Axis]
  Refine = true
  SideType = 0
  Suppressed = false
  Type = 0
  Type2 = 0
FEATURE [Sketcher::SketchObject] Sketch006
  ArcFitTolerance = 1e-06
  AttachmentSupport = -> [Pocket004]
  ExternalGeometry = -> [Pocket004]
  ExternalTypes = [0,0]
  FullyConstrained = true
  MakeInternals = false
  MapMode = 5
  Placement = pos=(0,-1.8e-15,-8) rot=(1,0,0;3.14159rad)
  sketch-geometry (2):
    g0: Circle CenterX=10 CenterY=26 CenterZ=0 NormalX=0 NormalY=0 NormalZ=1 AngleXU=0 Radius=4.75
    g1: Circle CenterX=10 CenterY=-26 CenterZ=0 NormalX=0 NormalY=0 NormalZ=1 AngleXU=0 Radius=4.75
  constraints (4):
    c: Coincident(g0,g-3)
    c: Coincident(g1,g-4)
    c: Equal(g1,g0)
    c: Diameter(g0) = 9.5
FEATURE [PartDesign::Pocket] Pocket005
  BaseFeature = -> Pocket004
  Direction = (0,0,1)
  Length = 1
  Length2 = 5
  Profile = -> Sketch006
  ReferenceAxis = -> Sketch006 [N_Axis]
  Refine = true
  SideType = 0
  Suppressed = false
  Type = 0
  Type2 = 0
FEATURE [PartDesign::Chamfer] Chamfer
  Angle = 45
  Base = -> Pocket005 [Edge4,Edge3]
  BaseFeature = -> Pocket005
  ChamferType = 0
  FlipDirection = false
  Refine = true
  Size = 3
  Size2 = 1
  SupportTransform = false
  Suppressed = false
  UseAllEdges = false
FEATURE [PartDesign::Chamfer] Chamfer001
  Angle = 45
  Base = -> Chamfer [Edge27,Edge24]
  BaseFeature = -> Chamfer
  ChamferType = 0
  FlipDirection = false
  Refine = true
  Size = 4
  Size2 = 1
  SupportTransform = false
  Suppressed = false
  UseAllEdges = false
FEATURE [PartDesign::Chamfer] Chamfer002
  Angle = 45
  Base = -> Chamfer001 [Edge29,Edge15]
  BaseFeature = -> Chamfer001
  ChamferType = 0
  FlipDirection = false
  Refine = true
  Size = 6
  Size2 = 1
  SupportTransform = false
  Suppressed = false
  UseAllEdges = false
FEATURE [PartDesign::Chamfer] Chamfer003
  Angle = 45
  Base = -> Chamfer002 [Edge49]
  BaseFeature = -> Chamfer002
  ChamferType = 0
  FlipDirection = false
  Refine = true
  Size = 3
  Size2 = 1
  SupportTransform = false
  Suppressed = false
  UseAllEdges = false
FEATURE [PartDesign::Chamfer] Chamfer004
  Angle = 45
  Base = -> Chamfer003 [Edge3]
  BaseFeature = -> Chamfer003
  ChamferType = 0
  FlipDirection = false
  Refine = true
  Size = 0.8
  Size2 = 1
  SupportTransform = false
  Suppressed = false
  UseAllEdges = false
FEATURE [PartDesign::Chamfer] Chamfer005
  Angle = 45
  Base = -> Chamfer004 [Edge80,Edge75]
  BaseFeature = -> Chamfer004
  ChamferType = 0
  FlipDirection = false
  Refine = true
  Size = 1
  Size2 = 1
  SupportTransform = false
  Suppressed = false
  UseAllEdges = false
FEATURE [PartDesign::Chamfer] Chamfer006
  Angle = 45
  Base = -> Chamfer005 [Edge83,Edge82,Edge80,Edge81]
  BaseFeature = -> Chamfer005
  ChamferType = 0
  FlipDirection = false
  Refine = true
  Size = 0.6
  Size2 = 1
  SupportTransform = false
  Suppressed = false
  UseAllEdges = false
FEATURE [PartDesign::Chamfer] Chamfer007
  Angle = 45
  Base = -> Chamfer006 [Face15,Face13]
  BaseFeature = -> Chamfer006
  ChamferType = 0
  FlipDirection = false
  Refine = true
  Size = 0.4
  Size2 = 1
  SupportTransform = false
  Suppressed = false
  UseAllEdges = false
FEATURE [PartDesign::Body] Body  label="free-wheel-support"
  AllowCompound = true
  Group = -> [Sketch,Pad,Sketch001,Pocket,Sketch002,Pocket001,Sketch003,Pocket002,Sketch004,Pocket003,Sketch005,Pocket004,Sketch006,Pocket005,Chamfer,Chamfer001,Chamfer002,Chamfer003,Chamfer004,Chamfer005,Chamfer006,Chamfer007]
  Origin = -> Origin
  Tip = -> Chamfer007
